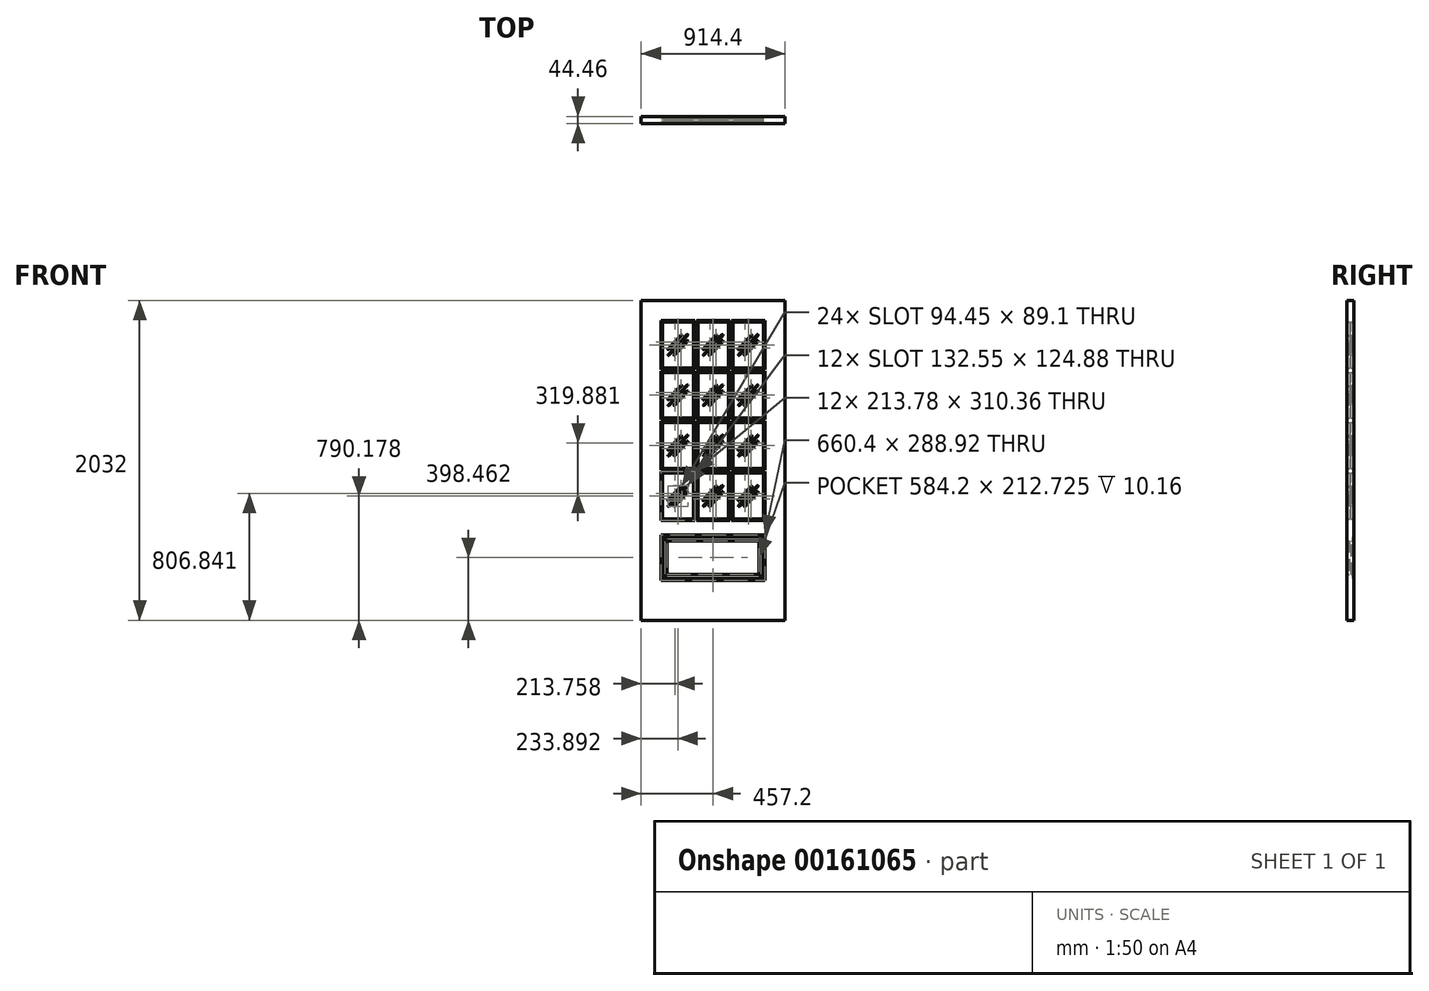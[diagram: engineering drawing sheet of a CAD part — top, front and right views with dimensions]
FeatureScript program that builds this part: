
annotation { "Feature Type Name" : "Feature", "Feature Type Description" : "" }
export const myFeature = defineFeature(function(context is Context, id is Id, definition is map)
    precondition{}
    {
        {
            var Q0;
            Q0=qCreatedBy(makeId("Front.planeOp"),FACE);
            var sketch = newSketch(context, id + "F0", { "sketchPlane" : qUnion([Q0])});
            skLineSegment(sketch, "E0.bottom", {"start": v(0, 2032) * mm, "end": v(914.4, 2032) * mm});
            skLineSegment(sketch, "E0.top", {"start": v(0, 0) * mm, "end": v(914.4, 0) * mm});
            skLineSegment(sketch, "E0.left", {"start": v(0, 2032) * mm, "end": v(0, 0) * mm});
            skLineSegment(sketch, "E0.right", {"start": v(914.4, 2032) * mm, "end": v(914.4, 0) * mm});
            skLineSegment(sketch, "E1.bottom", {"start": v(787.4, 254) * mm, "end": v(127, 254) * mm});
            skLineSegment(sketch, "E1.top", {"start": v(787.4, 542.93) * mm, "end": v(127, 542.93) * mm});
            skLineSegment(sketch, "E1.left", {"start": v(787.4, 254) * mm, "end": v(787.4, 542.93) * mm});
            skLineSegment(sketch, "E1.right", {"start": v(127, 254) * mm, "end": v(127, 542.93) * mm});
            skLineSegment(sketch, "E2.bottom", {"start": v(787.4, 635) * mm, "end": v(573.62, 635) * mm});
            skLineSegment(sketch, "E2.top", {"start": v(787.4, 945.36) * mm, "end": v(573.62, 945.36) * mm});
            skLineSegment(sketch, "E2.left", {"start": v(787.4, 635) * mm, "end": v(787.4, 945.36) * mm});
            skLineSegment(sketch, "E2.right", {"start": v(573.62, 635) * mm, "end": v(573.62, 945.36) * mm});
            skLineSegment(sketch, "E3.bottom", {"start": v(583.14, 935.83) * mm, "end": v(777.88, 935.83) * mm});
            skLineSegment(sketch, "E3.top", {"start": v(583.14, 644.53) * mm, "end": v(777.88, 644.53) * mm});
            skLineSegment(sketch, "E3.left", {"start": v(583.14, 935.83) * mm, "end": v(583.14, 644.53) * mm});
            skLineSegment(sketch, "E3.right", {"start": v(777.88, 935.83) * mm, "end": v(777.88, 644.53) * mm});
            skLineSegment(sketch, "E4", {"start": v(777.88, 935.83) * mm, "end": v(787.4, 945.36) * mm});
            skLineSegment(sketch, "E5", {"start": v(777.88, 644.52) * mm, "end": v(787.4, 635) * mm});
            skLineSegment(sketch, "E6", {"start": v(583.14, 644.53) * mm, "end": v(573.62, 635) * mm});
            skLineSegment(sketch, "E7", {"start": v(583.14, 935.83) * mm, "end": v(573.62, 945.36) * mm});
            skLineSegment(sketch, "E8", {"start": v(621.24, 727.08) * mm, "end": v(739.78, 853.28) * mm});
            skLineSegment(sketch, "E9", {"start": v(739.78, 815.18) * mm, "end": v(657.03, 727.08) * mm});
            skLineSegment(sketch, "E10.MirrorCS", {"start": v(701.75, 850.9) * mm, "end": v(619, 762.79) * mm});
            skLineSegment(sketch, "E11.0.1.1", {"start": v(583.14, 964.4) * mm, "end": v(777.88, 964.4) * mm});
            skLineSegment(sketch, "E11.0.1.2", {"start": v(701.75, 1170.78) * mm, "end": v(619, 1082.67) * mm});
            skLineSegment(sketch, "E11.0.1.3", {"start": v(787.4, 954.88) * mm, "end": v(573.62, 954.88) * mm});
            skLineSegment(sketch, "E11.0.1.4", {"start": v(583.14, 1255.71) * mm, "end": v(777.88, 1255.71) * mm});
            skLineSegment(sketch, "E11.0.1.7", {"start": v(621.24, 1046.96) * mm, "end": v(739.78, 1173.16) * mm});
            skLineSegment(sketch, "E11.0.1.9", {"start": v(573.62, 954.88) * mm, "end": v(573.62, 1265.24) * mm});
            skLineSegment(sketch, "E11.0.1.10", {"start": v(777.88, 1255.71) * mm, "end": v(777.88, 964.4) * mm});
            skLineSegment(sketch, "E11.0.1.11", {"start": v(787.4, 1265.24) * mm, "end": v(573.62, 1265.24) * mm});
            skLineSegment(sketch, "E11.0.1.12", {"start": v(739.78, 1135.06) * mm, "end": v(657.03, 1046.96) * mm});
            skLineSegment(sketch, "E11.0.1.13", {"start": v(787.4, 954.88) * mm, "end": v(787.4, 1265.24) * mm});
            skLineSegment(sketch, "E11.0.1.14", {"start": v(583.14, 1255.71) * mm, "end": v(583.14, 964.4) * mm});
            skLineSegment(sketch, "E11.0.1.15", {"start": v(777.88, 964.4) * mm, "end": v(787.4, 954.88) * mm});
            skLineSegment(sketch, "E11.0.1.16", {"start": v(777.87, 1255.71) * mm, "end": v(787.4, 1265.24) * mm});
            skLineSegment(sketch, "E11.0.1.17", {"start": v(583.14, 1255.71) * mm, "end": v(573.62, 1265.24) * mm});
            skLineSegment(sketch, "E11.0.1.18", {"start": v(583.14, 964.4) * mm, "end": v(573.62, 954.88) * mm});
            skLineSegment(sketch, "E11.0.2.1", {"start": v(583.14, 1284.29) * mm, "end": v(777.88, 1284.29) * mm});
            skLineSegment(sketch, "E11.0.2.2", {"start": v(701.75, 1490.66) * mm, "end": v(619, 1402.55) * mm});
            skLineSegment(sketch, "E11.0.2.3", {"start": v(787.4, 1274.76) * mm, "end": v(573.62, 1274.76) * mm});
            skLineSegment(sketch, "E11.0.2.4", {"start": v(583.14, 1575.6) * mm, "end": v(777.88, 1575.6) * mm});
            skLineSegment(sketch, "E11.0.2.7", {"start": v(621.24, 1366.84) * mm, "end": v(739.78, 1493.04) * mm});
            skLineSegment(sketch, "E11.0.2.9", {"start": v(573.62, 1274.76) * mm, "end": v(573.62, 1585.12) * mm});
            skLineSegment(sketch, "E11.0.2.10", {"start": v(777.88, 1575.6) * mm, "end": v(777.88, 1284.29) * mm});
            skLineSegment(sketch, "E11.0.2.11", {"start": v(787.4, 1585.12) * mm, "end": v(573.62, 1585.12) * mm});
            skLineSegment(sketch, "E11.0.2.12", {"start": v(739.77, 1454.94) * mm, "end": v(657.03, 1366.84) * mm});
            skLineSegment(sketch, "E11.0.2.13", {"start": v(787.4, 1274.76) * mm, "end": v(787.4, 1585.12) * mm});
            skLineSegment(sketch, "E11.0.2.14", {"start": v(583.14, 1575.6) * mm, "end": v(583.14, 1284.29) * mm});
            skLineSegment(sketch, "E11.0.2.15", {"start": v(777.88, 1284.29) * mm, "end": v(787.4, 1274.76) * mm});
            skLineSegment(sketch, "E11.0.2.16", {"start": v(777.87, 1575.6) * mm, "end": v(787.4, 1585.12) * mm});
            skLineSegment(sketch, "E11.0.2.17", {"start": v(583.14, 1575.6) * mm, "end": v(573.62, 1585.12) * mm});
            skLineSegment(sketch, "E11.0.2.18", {"start": v(583.14, 1284.29) * mm, "end": v(573.62, 1274.76) * mm});
            skLineSegment(sketch, "E11.1.0.1", {"start": v(359.83, 644.53) * mm, "end": v(554.57, 644.53) * mm});
            skLineSegment(sketch, "E11.1.0.2", {"start": v(478.44, 850.9) * mm, "end": v(395.7, 762.79) * mm});
            skLineSegment(sketch, "E11.1.0.3", {"start": v(564.1, 635) * mm, "end": v(350.3, 635) * mm});
            skLineSegment(sketch, "E11.1.0.4", {"start": v(359.83, 935.83) * mm, "end": v(554.57, 935.83) * mm});
            skLineSegment(sketch, "E11.1.0.7", {"start": v(397.93, 727.08) * mm, "end": v(516.47, 853.28) * mm});
            skLineSegment(sketch, "E11.1.0.9", {"start": v(350.3, 635) * mm, "end": v(350.3, 945.36) * mm});
            skLineSegment(sketch, "E11.1.0.10", {"start": v(554.57, 935.83) * mm, "end": v(554.57, 644.52) * mm});
            skLineSegment(sketch, "E11.1.0.11", {"start": v(564.1, 945.36) * mm, "end": v(350.3, 945.36) * mm});
            skLineSegment(sketch, "E11.1.0.12", {"start": v(516.47, 815.18) * mm, "end": v(433.72, 727.08) * mm});
            skLineSegment(sketch, "E11.1.0.13", {"start": v(564.1, 635) * mm, "end": v(564.1, 945.36) * mm});
            skLineSegment(sketch, "E11.1.0.14", {"start": v(359.83, 935.83) * mm, "end": v(359.83, 644.52) * mm});
            skLineSegment(sketch, "E11.1.0.15", {"start": v(554.57, 644.52) * mm, "end": v(564.1, 635) * mm});
            skLineSegment(sketch, "E11.1.0.16", {"start": v(554.57, 935.83) * mm, "end": v(564.1, 945.36) * mm});
            skLineSegment(sketch, "E11.1.0.17", {"start": v(359.83, 935.83) * mm, "end": v(350.3, 945.36) * mm});
            skLineSegment(sketch, "E11.1.0.18", {"start": v(359.83, 644.52) * mm, "end": v(350.3, 635) * mm});
            skLineSegment(sketch, "E11.1.1.1", {"start": v(359.83, 964.4) * mm, "end": v(554.57, 964.4) * mm});
            skLineSegment(sketch, "E11.1.1.2", {"start": v(478.44, 1170.78) * mm, "end": v(395.7, 1082.67) * mm});
            skLineSegment(sketch, "E11.1.1.3", {"start": v(564.1, 954.88) * mm, "end": v(350.3, 954.88) * mm});
            skLineSegment(sketch, "E11.1.1.4", {"start": v(359.83, 1255.71) * mm, "end": v(554.57, 1255.71) * mm});
            skLineSegment(sketch, "E11.1.1.7", {"start": v(397.93, 1046.96) * mm, "end": v(516.47, 1173.16) * mm});
            skLineSegment(sketch, "E11.1.1.9", {"start": v(350.3, 954.88) * mm, "end": v(350.3, 1265.24) * mm});
            skLineSegment(sketch, "E11.1.1.10", {"start": v(554.57, 1255.71) * mm, "end": v(554.57, 964.4) * mm});
            skLineSegment(sketch, "E11.1.1.11", {"start": v(564.1, 1265.24) * mm, "end": v(350.3, 1265.24) * mm});
            skLineSegment(sketch, "E11.1.1.12", {"start": v(516.47, 1135.06) * mm, "end": v(433.72, 1046.96) * mm});
            skLineSegment(sketch, "E11.1.1.13", {"start": v(564.1, 954.88) * mm, "end": v(564.1, 1265.24) * mm});
            skLineSegment(sketch, "E11.1.1.14", {"start": v(359.83, 1255.71) * mm, "end": v(359.83, 964.4) * mm});
            skLineSegment(sketch, "E11.1.1.15", {"start": v(554.57, 964.4) * mm, "end": v(564.1, 954.88) * mm});
            skLineSegment(sketch, "E11.1.1.16", {"start": v(554.57, 1255.71) * mm, "end": v(564.1, 1265.24) * mm});
            skLineSegment(sketch, "E11.1.1.17", {"start": v(359.83, 1255.71) * mm, "end": v(350.3, 1265.24) * mm});
            skLineSegment(sketch, "E11.1.1.18", {"start": v(359.83, 964.4) * mm, "end": v(350.3, 954.88) * mm});
            skLineSegment(sketch, "E11.1.2.1", {"start": v(359.83, 1284.29) * mm, "end": v(554.57, 1284.29) * mm});
            skLineSegment(sketch, "E11.1.2.2", {"start": v(478.44, 1490.66) * mm, "end": v(395.7, 1402.55) * mm});
            skLineSegment(sketch, "E11.1.2.3", {"start": v(564.1, 1274.76) * mm, "end": v(350.3, 1274.76) * mm});
            skLineSegment(sketch, "E11.1.2.4", {"start": v(359.83, 1575.6) * mm, "end": v(554.57, 1575.6) * mm});
            skLineSegment(sketch, "E11.1.2.7", {"start": v(397.93, 1366.84) * mm, "end": v(516.47, 1493.04) * mm});
            skLineSegment(sketch, "E11.1.2.9", {"start": v(350.3, 1274.76) * mm, "end": v(350.3, 1585.12) * mm});
            skLineSegment(sketch, "E11.1.2.10", {"start": v(554.57, 1575.6) * mm, "end": v(554.57, 1284.29) * mm});
            skLineSegment(sketch, "E11.1.2.11", {"start": v(564.1, 1585.12) * mm, "end": v(350.3, 1585.12) * mm});
            skLineSegment(sketch, "E11.1.2.12", {"start": v(516.47, 1454.94) * mm, "end": v(433.72, 1366.84) * mm});
            skLineSegment(sketch, "E11.1.2.13", {"start": v(564.1, 1274.76) * mm, "end": v(564.1, 1585.12) * mm});
            skLineSegment(sketch, "E11.1.2.14", {"start": v(359.83, 1575.6) * mm, "end": v(359.83, 1284.29) * mm});
            skLineSegment(sketch, "E11.1.2.15", {"start": v(554.57, 1284.29) * mm, "end": v(564.1, 1274.76) * mm});
            skLineSegment(sketch, "E11.1.2.16", {"start": v(554.57, 1575.6) * mm, "end": v(564.1, 1585.12) * mm});
            skLineSegment(sketch, "E11.1.2.17", {"start": v(359.83, 1575.6) * mm, "end": v(350.3, 1585.12) * mm});
            skLineSegment(sketch, "E11.1.2.18", {"start": v(359.83, 1284.29) * mm, "end": v(350.3, 1274.76) * mm});
            skLineSegment(sketch, "E11.2.0.1", {"start": v(136.53, 644.53) * mm, "end": v(331.26, 644.53) * mm});
            skLineSegment(sketch, "E11.2.0.2", {"start": v(255.13, 850.9) * mm, "end": v(172.38, 762.79) * mm});
            skLineSegment(sketch, "E11.2.0.3", {"start": v(340.78, 635) * mm, "end": v(127, 635) * mm});
            skLineSegment(sketch, "E11.2.0.4", {"start": v(136.52, 935.83) * mm, "end": v(331.26, 935.83) * mm});
            skLineSegment(sketch, "E11.2.0.7", {"start": v(174.63, 727.08) * mm, "end": v(293.16, 853.28) * mm});
            skLineSegment(sketch, "E11.2.0.9", {"start": v(127, 635) * mm, "end": v(127, 945.36) * mm});
            skLineSegment(sketch, "E11.2.0.10", {"start": v(331.26, 935.83) * mm, "end": v(331.26, 644.52) * mm});
            skLineSegment(sketch, "E11.2.0.11", {"start": v(340.78, 945.36) * mm, "end": v(127, 945.36) * mm});
            skLineSegment(sketch, "E11.2.0.12", {"start": v(293.16, 815.18) * mm, "end": v(210.4, 727.08) * mm});
            skLineSegment(sketch, "E11.2.0.13", {"start": v(340.78, 635) * mm, "end": v(340.78, 945.36) * mm});
            skLineSegment(sketch, "E11.2.0.14", {"start": v(136.52, 935.83) * mm, "end": v(136.52, 644.52) * mm});
            skLineSegment(sketch, "E11.2.0.15", {"start": v(331.26, 644.52) * mm, "end": v(340.78, 635) * mm});
            skLineSegment(sketch, "E11.2.0.16", {"start": v(331.26, 935.83) * mm, "end": v(340.78, 945.36) * mm});
            skLineSegment(sketch, "E11.2.0.17", {"start": v(136.52, 935.83) * mm, "end": v(127, 945.36) * mm});
            skLineSegment(sketch, "E11.2.0.18", {"start": v(136.52, 644.52) * mm, "end": v(127, 635) * mm});
            skLineSegment(sketch, "E11.2.1.1", {"start": v(136.52, 964.4) * mm, "end": v(331.26, 964.4) * mm});
            skLineSegment(sketch, "E11.2.1.2", {"start": v(255.13, 1170.78) * mm, "end": v(172.38, 1082.67) * mm});
            skLineSegment(sketch, "E11.2.1.3", {"start": v(340.78, 954.88) * mm, "end": v(127, 954.88) * mm});
            skLineSegment(sketch, "E11.2.1.4", {"start": v(136.52, 1255.71) * mm, "end": v(331.26, 1255.71) * mm});
            skLineSegment(sketch, "E11.2.1.7", {"start": v(174.63, 1046.96) * mm, "end": v(293.16, 1173.16) * mm});
            skLineSegment(sketch, "E11.2.1.9", {"start": v(127, 954.88) * mm, "end": v(127, 1265.24) * mm});
            skLineSegment(sketch, "E11.2.1.10", {"start": v(331.26, 1255.71) * mm, "end": v(331.26, 964.4) * mm});
            skLineSegment(sketch, "E11.2.1.11", {"start": v(340.78, 1265.24) * mm, "end": v(127, 1265.24) * mm});
            skLineSegment(sketch, "E11.2.1.12", {"start": v(293.16, 1135.06) * mm, "end": v(210.4, 1046.96) * mm});
            skLineSegment(sketch, "E11.2.1.13", {"start": v(340.78, 954.88) * mm, "end": v(340.78, 1265.24) * mm});
            skLineSegment(sketch, "E11.2.1.14", {"start": v(136.52, 1255.71) * mm, "end": v(136.52, 964.4) * mm});
            skLineSegment(sketch, "E11.2.1.15", {"start": v(331.26, 964.4) * mm, "end": v(340.78, 954.88) * mm});
            skLineSegment(sketch, "E11.2.1.16", {"start": v(331.26, 1255.71) * mm, "end": v(340.78, 1265.24) * mm});
            skLineSegment(sketch, "E11.2.1.17", {"start": v(136.52, 1255.71) * mm, "end": v(127, 1265.24) * mm});
            skLineSegment(sketch, "E11.2.1.18", {"start": v(136.52, 964.4) * mm, "end": v(127, 954.88) * mm});
            skLineSegment(sketch, "E11.2.2.1", {"start": v(136.52, 1284.29) * mm, "end": v(331.26, 1284.29) * mm});
            skLineSegment(sketch, "E11.2.2.2", {"start": v(255.13, 1490.66) * mm, "end": v(172.38, 1402.55) * mm});
            skLineSegment(sketch, "E11.2.2.3", {"start": v(340.78, 1274.76) * mm, "end": v(127, 1274.76) * mm});
            skLineSegment(sketch, "E11.2.2.4", {"start": v(136.52, 1575.6) * mm, "end": v(331.26, 1575.6) * mm});
            skLineSegment(sketch, "E11.2.2.7", {"start": v(174.63, 1366.84) * mm, "end": v(293.16, 1493.04) * mm});
            skLineSegment(sketch, "E11.2.2.9", {"start": v(127, 1274.76) * mm, "end": v(127, 1585.12) * mm});
            skLineSegment(sketch, "E11.2.2.10", {"start": v(331.26, 1575.6) * mm, "end": v(331.26, 1284.29) * mm});
            skLineSegment(sketch, "E11.2.2.11", {"start": v(340.78, 1585.12) * mm, "end": v(127, 1585.12) * mm});
            skLineSegment(sketch, "E11.2.2.12", {"start": v(293.16, 1454.94) * mm, "end": v(210.4, 1366.84) * mm});
            skLineSegment(sketch, "E11.2.2.13", {"start": v(340.78, 1274.76) * mm, "end": v(340.78, 1585.12) * mm});
            skLineSegment(sketch, "E11.2.2.14", {"start": v(136.52, 1575.6) * mm, "end": v(136.52, 1284.29) * mm});
            skLineSegment(sketch, "E11.2.2.15", {"start": v(331.26, 1284.29) * mm, "end": v(340.78, 1274.76) * mm});
            skLineSegment(sketch, "E11.2.2.16", {"start": v(331.26, 1575.6) * mm, "end": v(340.78, 1585.12) * mm});
            skLineSegment(sketch, "E11.2.2.17", {"start": v(136.52, 1575.6) * mm, "end": v(127, 1585.12) * mm});
            skLineSegment(sketch, "E11.2.2.18", {"start": v(136.52, 1284.29) * mm, "end": v(127, 1274.76) * mm});
            skLineSegment(sketch, "E11.direction1", {"start": v(573.62, 635) * mm, "end": v(350.3, 635) * mm, "construction": true});
            skLineSegment(sketch, "E11.direction2", {"start": v(573.62, 635) * mm, "end": v(573.62, 954.88) * mm, "construction": true});
            skLineSegment(sketch, "E12.3.0.3", {"start": v(583.14, 1604.17) * mm, "end": v(777.88, 1604.17) * mm});
            skLineSegment(sketch, "E12.6.0.3", {"start": v(701.75, 1810.54) * mm, "end": v(619, 1722.43) * mm});
            skLineSegment(sketch, "E12.9.0.3", {"start": v(787.4, 1594.64) * mm, "end": v(573.62, 1594.64) * mm});
            skLineSegment(sketch, "E12.12.0.3", {"start": v(583.14, 1895.48) * mm, "end": v(777.88, 1895.48) * mm});
            skLineSegment(sketch, "E12.21.0.3", {"start": v(621.24, 1686.72) * mm, "end": v(739.77, 1812.92) * mm});
            skLineSegment(sketch, "E12.27.0.3", {"start": v(573.62, 1594.64) * mm, "end": v(573.62, 1905) * mm});
            skLineSegment(sketch, "E12.30.0.3", {"start": v(777.88, 1895.48) * mm, "end": v(777.88, 1604.17) * mm});
            skLineSegment(sketch, "E12.33.0.3", {"start": v(787.4, 1905) * mm, "end": v(573.62, 1905) * mm});
            skLineSegment(sketch, "E12.36.0.3", {"start": v(739.77, 1774.82) * mm, "end": v(657.03, 1686.72) * mm});
            skLineSegment(sketch, "E12.39.0.3", {"start": v(787.4, 1594.64) * mm, "end": v(787.4, 1905) * mm});
            skLineSegment(sketch, "E12.42.0.3", {"start": v(583.14, 1895.48) * mm, "end": v(583.14, 1604.17) * mm});
            skLineSegment(sketch, "E12.45.0.3", {"start": v(777.88, 1604.17) * mm, "end": v(787.4, 1594.64) * mm});
            skLineSegment(sketch, "E12.48.0.3", {"start": v(777.88, 1895.47) * mm, "end": v(787.4, 1905) * mm});
            skLineSegment(sketch, "E12.51.0.3", {"start": v(583.14, 1895.48) * mm, "end": v(573.62, 1905) * mm});
            skLineSegment(sketch, "E12.54.0.3", {"start": v(583.14, 1604.17) * mm, "end": v(573.62, 1594.64) * mm});
            skLineSegment(sketch, "E12.3.1.3", {"start": v(359.83, 1604.17) * mm, "end": v(554.57, 1604.17) * mm});
            skLineSegment(sketch, "E12.6.1.3", {"start": v(478.44, 1810.54) * mm, "end": v(395.7, 1722.43) * mm});
            skLineSegment(sketch, "E12.9.1.3", {"start": v(564.1, 1594.64) * mm, "end": v(350.3, 1594.64) * mm});
            skLineSegment(sketch, "E12.12.1.3", {"start": v(359.83, 1895.48) * mm, "end": v(554.57, 1895.48) * mm});
            skLineSegment(sketch, "E12.21.1.3", {"start": v(397.93, 1686.72) * mm, "end": v(516.47, 1812.92) * mm});
            skLineSegment(sketch, "E12.27.1.3", {"start": v(350.3, 1594.64) * mm, "end": v(350.3, 1905) * mm});
            skLineSegment(sketch, "E12.30.1.3", {"start": v(554.57, 1895.48) * mm, "end": v(554.57, 1604.17) * mm});
            skLineSegment(sketch, "E12.33.1.3", {"start": v(564.1, 1905) * mm, "end": v(350.3, 1905) * mm});
            skLineSegment(sketch, "E12.36.1.3", {"start": v(516.47, 1774.82) * mm, "end": v(433.72, 1686.72) * mm});
            skLineSegment(sketch, "E12.39.1.3", {"start": v(564.1, 1594.64) * mm, "end": v(564.1, 1905) * mm});
            skLineSegment(sketch, "E12.42.1.3", {"start": v(359.83, 1895.48) * mm, "end": v(359.83, 1604.17) * mm});
            skLineSegment(sketch, "E12.45.1.3", {"start": v(554.57, 1604.17) * mm, "end": v(564.1, 1594.64) * mm});
            skLineSegment(sketch, "E12.48.1.3", {"start": v(554.57, 1895.47) * mm, "end": v(564.1, 1905) * mm});
            skLineSegment(sketch, "E12.51.1.3", {"start": v(359.83, 1895.48) * mm, "end": v(350.3, 1905) * mm});
            skLineSegment(sketch, "E12.54.1.3", {"start": v(359.83, 1604.17) * mm, "end": v(350.3, 1594.64) * mm});
            skLineSegment(sketch, "E12.3.2.3", {"start": v(136.52, 1604.17) * mm, "end": v(331.26, 1604.17) * mm});
            skLineSegment(sketch, "E12.6.2.3", {"start": v(255.13, 1810.54) * mm, "end": v(172.38, 1722.43) * mm});
            skLineSegment(sketch, "E12.9.2.3", {"start": v(340.78, 1594.64) * mm, "end": v(127, 1594.64) * mm});
            skLineSegment(sketch, "E12.12.2.3", {"start": v(136.52, 1895.48) * mm, "end": v(331.26, 1895.48) * mm});
            skLineSegment(sketch, "E12.21.2.3", {"start": v(174.63, 1686.72) * mm, "end": v(293.16, 1812.92) * mm});
            skLineSegment(sketch, "E12.27.2.3", {"start": v(127, 1594.64) * mm, "end": v(127, 1905) * mm});
            skLineSegment(sketch, "E12.30.2.3", {"start": v(331.26, 1895.48) * mm, "end": v(331.26, 1604.17) * mm});
            skLineSegment(sketch, "E12.33.2.3", {"start": v(340.78, 1905) * mm, "end": v(127, 1905) * mm});
            skLineSegment(sketch, "E12.36.2.3", {"start": v(293.16, 1774.82) * mm, "end": v(210.4, 1686.72) * mm});
            skLineSegment(sketch, "E12.39.2.3", {"start": v(340.78, 1594.64) * mm, "end": v(340.78, 1905) * mm});
            skLineSegment(sketch, "E12.42.2.3", {"start": v(136.52, 1895.48) * mm, "end": v(136.52, 1604.17) * mm});
            skLineSegment(sketch, "E12.45.2.3", {"start": v(331.26, 1604.17) * mm, "end": v(340.78, 1594.64) * mm});
            skLineSegment(sketch, "E12.48.2.3", {"start": v(331.26, 1895.47) * mm, "end": v(340.78, 1905) * mm});
            skLineSegment(sketch, "E12.51.2.3", {"start": v(136.52, 1895.48) * mm, "end": v(127, 1905) * mm});
            skLineSegment(sketch, "E12.54.2.3", {"start": v(136.52, 1604.17) * mm, "end": v(127, 1594.64) * mm});
            skLineSegment(sketch, "E13.0", {"start": v(774.7, 530.22) * mm, "end": v(139.7, 530.22) * mm});
            skLineSegment(sketch, "E13.1", {"start": v(774.7, 266.7) * mm, "end": v(774.7, 530.22) * mm});
            skLineSegment(sketch, "E13.2", {"start": v(774.7, 266.7) * mm, "end": v(139.7, 266.7) * mm});
            skLineSegment(sketch, "E13.3", {"start": v(139.7, 266.7) * mm, "end": v(139.7, 530.22) * mm});
            skLineSegment(sketch, "E14.0", {"start": v(749.3, 292.1) * mm, "end": v(165.1, 292.1) * mm});
            skLineSegment(sketch, "E14.1", {"start": v(749.3, 292.1) * mm, "end": v(749.3, 504.83) * mm});
            skLineSegment(sketch, "E14.2", {"start": v(749.3, 504.83) * mm, "end": v(165.1, 504.83) * mm});
            skLineSegment(sketch, "E14.3", {"start": v(165.1, 292.1) * mm, "end": v(165.1, 504.83) * mm});
            skSolve(sketch);
        }
        {
            var Q0;
            Q0=qCreatedBy(makeId("Front.planeOp"),FACE);
            var sketch = newSketch(context, id + "F1", { "sketchPlane" : qUnion([Q0])});
            skLineSegment(sketch, "E15.bottom", {"start": v(0, 2032) * mm, "end": v(914.4, 2032) * mm});
            skLineSegment(sketch, "E15.top", {"start": v(0, 0) * mm, "end": v(914.4, 0) * mm});
            skLineSegment(sketch, "E15.left", {"start": v(0, 2032) * mm, "end": v(0, 0) * mm});
            skLineSegment(sketch, "E15.right", {"start": v(914.4, 2032) * mm, "end": v(914.4, 0) * mm});
            skLineSegment(sketch, "E16.bottom", {"start": v(127, 542.93) * mm, "end": v(787.4, 542.93) * mm});
            skLineSegment(sketch, "E16.top", {"start": v(127, 254) * mm, "end": v(787.4, 254) * mm});
            skLineSegment(sketch, "E16.left", {"start": v(127, 542.93) * mm, "end": v(127, 254) * mm});
            skLineSegment(sketch, "E16.right", {"start": v(787.4, 542.93) * mm, "end": v(787.4, 254) * mm});
            skLineSegment(sketch, "E17.bottom", {"start": v(127, 635) * mm, "end": v(340.78, 635) * mm});
            skLineSegment(sketch, "E17.top", {"start": v(127, 945.36) * mm, "end": v(340.78, 945.36) * mm});
            skLineSegment(sketch, "E17.left", {"start": v(127, 635) * mm, "end": v(127, 945.36) * mm});
            skLineSegment(sketch, "E17.right", {"start": v(340.78, 635) * mm, "end": v(340.78, 945.36) * mm});
            skLineSegment(sketch, "E18.bottom", {"start": v(350.3, 945.36) * mm, "end": v(564.1, 945.36) * mm});
            skLineSegment(sketch, "E18.top", {"start": v(350.3, 635) * mm, "end": v(564.1, 635) * mm});
            skLineSegment(sketch, "E18.left", {"start": v(350.3, 945.36) * mm, "end": v(350.3, 635) * mm});
            skLineSegment(sketch, "E18.right", {"start": v(564.1, 945.36) * mm, "end": v(564.1, 635) * mm});
            skLineSegment(sketch, "E19.bottom", {"start": v(573.62, 945.36) * mm, "end": v(787.4, 945.36) * mm});
            skLineSegment(sketch, "E19.top", {"start": v(573.62, 635) * mm, "end": v(787.4, 635) * mm});
            skLineSegment(sketch, "E19.left", {"start": v(573.62, 945.36) * mm, "end": v(573.62, 635) * mm});
            skLineSegment(sketch, "E19.right", {"start": v(787.4, 945.36) * mm, "end": v(787.4, 635) * mm});
            skLineSegment(sketch, "E20.bottom", {"start": v(573.62, 954.88) * mm, "end": v(787.4, 954.88) * mm});
            skLineSegment(sketch, "E20.top", {"start": v(573.62, 1265.24) * mm, "end": v(787.4, 1265.24) * mm});
            skLineSegment(sketch, "E20.left", {"start": v(573.62, 954.88) * mm, "end": v(573.62, 1265.24) * mm});
            skLineSegment(sketch, "E20.right", {"start": v(787.4, 954.88) * mm, "end": v(787.4, 1265.24) * mm});
            skLineSegment(sketch, "E21.bottom", {"start": v(350.3, 1265.24) * mm, "end": v(564.1, 1265.24) * mm});
            skLineSegment(sketch, "E21.top", {"start": v(350.3, 954.88) * mm, "end": v(564.1, 954.88) * mm});
            skLineSegment(sketch, "E21.left", {"start": v(350.3, 1265.24) * mm, "end": v(350.3, 954.88) * mm});
            skLineSegment(sketch, "E21.right", {"start": v(564.1, 1265.24) * mm, "end": v(564.1, 954.88) * mm});
            skLineSegment(sketch, "E22.bottom", {"start": v(340.78, 1265.24) * mm, "end": v(127, 1265.24) * mm});
            skLineSegment(sketch, "E22.top", {"start": v(340.78, 954.88) * mm, "end": v(127, 954.88) * mm});
            skLineSegment(sketch, "E22.left", {"start": v(340.78, 1265.24) * mm, "end": v(340.78, 954.88) * mm});
            skLineSegment(sketch, "E22.right", {"start": v(127, 1265.24) * mm, "end": v(127, 954.88) * mm});
            skLineSegment(sketch, "E23.bottom", {"start": v(127, 1274.76) * mm, "end": v(340.78, 1274.76) * mm});
            skLineSegment(sketch, "E23.top", {"start": v(127, 1585.12) * mm, "end": v(340.78, 1585.12) * mm});
            skLineSegment(sketch, "E23.left", {"start": v(127, 1274.76) * mm, "end": v(127, 1585.12) * mm});
            skLineSegment(sketch, "E23.right", {"start": v(340.78, 1274.76) * mm, "end": v(340.78, 1585.12) * mm});
            skLineSegment(sketch, "E24.bottom", {"start": v(350.3, 1585.12) * mm, "end": v(564.1, 1585.12) * mm});
            skLineSegment(sketch, "E24.top", {"start": v(350.3, 1274.76) * mm, "end": v(564.1, 1274.76) * mm});
            skLineSegment(sketch, "E24.left", {"start": v(350.3, 1585.12) * mm, "end": v(350.3, 1274.76) * mm});
            skLineSegment(sketch, "E24.right", {"start": v(564.1, 1585.12) * mm, "end": v(564.1, 1274.76) * mm});
            skLineSegment(sketch, "E25.bottom", {"start": v(573.62, 1585.12) * mm, "end": v(787.4, 1585.12) * mm});
            skLineSegment(sketch, "E25.top", {"start": v(573.62, 1274.76) * mm, "end": v(787.4, 1274.76) * mm});
            skLineSegment(sketch, "E25.left", {"start": v(573.62, 1585.12) * mm, "end": v(573.62, 1274.76) * mm});
            skLineSegment(sketch, "E25.right", {"start": v(787.4, 1585.12) * mm, "end": v(787.4, 1274.76) * mm});
            skLineSegment(sketch, "E26.bottom", {"start": v(573.62, 1594.64) * mm, "end": v(787.4, 1594.64) * mm});
            skLineSegment(sketch, "E26.top", {"start": v(573.62, 1905) * mm, "end": v(787.4, 1905) * mm});
            skLineSegment(sketch, "E26.left", {"start": v(573.62, 1594.64) * mm, "end": v(573.62, 1905) * mm});
            skLineSegment(sketch, "E26.right", {"start": v(787.4, 1594.64) * mm, "end": v(787.4, 1905) * mm});
            skLineSegment(sketch, "E27.bottom", {"start": v(564.1, 1905) * mm, "end": v(350.3, 1905) * mm});
            skLineSegment(sketch, "E27.top", {"start": v(564.1, 1594.64) * mm, "end": v(350.3, 1594.64) * mm});
            skLineSegment(sketch, "E27.left", {"start": v(564.1, 1905) * mm, "end": v(564.1, 1594.64) * mm});
            skLineSegment(sketch, "E27.right", {"start": v(350.3, 1905) * mm, "end": v(350.3, 1594.64) * mm});
            skLineSegment(sketch, "E28.bottom", {"start": v(340.78, 1594.64) * mm, "end": v(127, 1594.64) * mm});
            skLineSegment(sketch, "E28.top", {"start": v(340.78, 1905) * mm, "end": v(127, 1905) * mm});
            skLineSegment(sketch, "E28.left", {"start": v(340.78, 1594.64) * mm, "end": v(340.78, 1905) * mm});
            skLineSegment(sketch, "E28.right", {"start": v(127, 1594.64) * mm, "end": v(127, 1905) * mm});
            skSolve(sketch);
        }
        {
            var Q0;
            Q0=qSketchRegion(id+"F1",true);
            extrude(context, id + "F2", {"entities" : qUnion([Q0]), "depth" : 22.22 * mm, "hasSecondDirection" : true, "secondDirectionOppositeDirection" : true, "secondDirectionDepth" : 22.22 * mm});
        }
        {
            var Q0;
            Q0=qCreatedBy(makeId("Front.planeOp"),FACE);
            var sketch = newSketch(context, id + "F3", { "sketchPlane" : qUnion([Q0])});
            skLineSegment(sketch, "E29.0", {"start": v(787.4, 1594.64) * mm, "end": v(787.4, 1905) * mm});
            skLineSegment(sketch, "E30.0", {"start": v(777.88, 1895.47) * mm, "end": v(787.4, 1905) * mm});
            skLineSegment(sketch, "E31.0", {"start": v(777.88, 1895.48) * mm, "end": v(777.88, 1604.17) * mm});
            skLineSegment(sketch, "E32.0", {"start": v(777.88, 1604.17) * mm, "end": v(787.4, 1594.64) * mm});
            skLineSegment(sketch, "E33.0", {"start": v(583.14, 1604.17) * mm, "end": v(573.62, 1594.64) * mm});
            skLineSegment(sketch, "E34.0", {"start": v(583.14, 1895.48) * mm, "end": v(583.14, 1604.17) * mm});
            skLineSegment(sketch, "E35.0", {"start": v(583.14, 1895.48) * mm, "end": v(573.62, 1905) * mm});
            skLineSegment(sketch, "E36.0", {"start": v(573.62, 1594.64) * mm, "end": v(573.62, 1905) * mm});
            skLineSegment(sketch, "E37.0", {"start": v(564.1, 1594.64) * mm, "end": v(564.1, 1905) * mm});
            skLineSegment(sketch, "E38.0", {"start": v(554.57, 1895.47) * mm, "end": v(564.1, 1905) * mm});
            skLineSegment(sketch, "E39.0", {"start": v(554.57, 1895.48) * mm, "end": v(554.57, 1604.17) * mm});
            skLineSegment(sketch, "E40.0", {"start": v(554.57, 1604.17) * mm, "end": v(564.1, 1594.64) * mm});
            skLineSegment(sketch, "E41.0", {"start": v(359.83, 1604.17) * mm, "end": v(350.3, 1594.64) * mm});
            skLineSegment(sketch, "E42.0", {"start": v(359.83, 1895.48) * mm, "end": v(359.83, 1604.17) * mm});
            skLineSegment(sketch, "E43.0", {"start": v(350.3, 1594.64) * mm, "end": v(350.3, 1905) * mm});
            skLineSegment(sketch, "E44.0", {"start": v(359.83, 1895.48) * mm, "end": v(350.3, 1905) * mm});
            skLineSegment(sketch, "E45.0", {"start": v(331.26, 1895.47) * mm, "end": v(340.78, 1905) * mm});
            skLineSegment(sketch, "E46.0", {"start": v(340.78, 1594.64) * mm, "end": v(340.78, 1905) * mm});
            skLineSegment(sketch, "E47.0", {"start": v(331.26, 1604.17) * mm, "end": v(340.78, 1594.64) * mm});
            skLineSegment(sketch, "E48.0", {"start": v(331.26, 1895.48) * mm, "end": v(331.26, 1604.17) * mm});
            skLineSegment(sketch, "E49.0", {"start": v(136.52, 1895.48) * mm, "end": v(127, 1905) * mm});
            skLineSegment(sketch, "E50.0", {"start": v(136.52, 1895.48) * mm, "end": v(136.52, 1604.17) * mm});
            skLineSegment(sketch, "E51.0", {"start": v(127, 1594.64) * mm, "end": v(127, 1905) * mm});
            skLineSegment(sketch, "E52.0", {"start": v(136.52, 1604.17) * mm, "end": v(127, 1594.64) * mm});
            skLineSegment(sketch, "E53.0", {"start": v(787.4, 1274.76) * mm, "end": v(787.4, 1585.12) * mm});
            skLineSegment(sketch, "E54.0", {"start": v(777.88, 1575.6) * mm, "end": v(777.88, 1284.29) * mm});
            skLineSegment(sketch, "E55.0", {"start": v(777.88, 1284.29) * mm, "end": v(787.4, 1274.76) * mm});
            skLineSegment(sketch, "E56.0", {"start": v(777.87, 1575.6) * mm, "end": v(787.4, 1585.12) * mm});
            skLineSegment(sketch, "E57.0", {"start": v(583.14, 1575.6) * mm, "end": v(573.62, 1585.12) * mm});
            skLineSegment(sketch, "E58.0", {"start": v(573.62, 1274.76) * mm, "end": v(573.62, 1585.12) * mm});
            skLineSegment(sketch, "E59.0", {"start": v(583.14, 1575.6) * mm, "end": v(583.14, 1284.29) * mm});
            skLineSegment(sketch, "E60.0", {"start": v(583.14, 1284.29) * mm, "end": v(573.62, 1274.76) * mm});
            skLineSegment(sketch, "E61.0", {"start": v(554.57, 1284.29) * mm, "end": v(564.1, 1274.76) * mm});
            skLineSegment(sketch, "E62.0", {"start": v(564.1, 1274.76) * mm, "end": v(564.1, 1585.12) * mm});
            skLineSegment(sketch, "E63.0", {"start": v(554.57, 1575.6) * mm, "end": v(554.57, 1284.29) * mm});
            skLineSegment(sketch, "E64.0", {"start": v(554.57, 1575.6) * mm, "end": v(564.1, 1585.12) * mm});
            skLineSegment(sketch, "E65.0", {"start": v(359.83, 1575.6) * mm, "end": v(350.3, 1585.12) * mm});
            skLineSegment(sketch, "E66.0", {"start": v(359.83, 1575.6) * mm, "end": v(359.83, 1284.29) * mm});
            skLineSegment(sketch, "E67.0", {"start": v(350.3, 1274.76) * mm, "end": v(350.3, 1585.12) * mm});
            skLineSegment(sketch, "E68.0", {"start": v(359.83, 1284.29) * mm, "end": v(350.3, 1274.76) * mm});
            skLineSegment(sketch, "E69.0", {"start": v(331.26, 1284.29) * mm, "end": v(340.78, 1274.76) * mm});
            skLineSegment(sketch, "E70.0", {"start": v(340.78, 1274.76) * mm, "end": v(340.78, 1585.12) * mm});
            skLineSegment(sketch, "E71.0", {"start": v(331.26, 1575.6) * mm, "end": v(331.26, 1284.29) * mm});
            skLineSegment(sketch, "E72.0", {"start": v(331.26, 1575.6) * mm, "end": v(340.78, 1585.12) * mm});
            skLineSegment(sketch, "E73.0", {"start": v(136.52, 1575.6) * mm, "end": v(127, 1585.12) * mm});
            skLineSegment(sketch, "E74.0", {"start": v(136.52, 1575.6) * mm, "end": v(136.52, 1284.29) * mm});
            skLineSegment(sketch, "E75.0", {"start": v(127, 1274.76) * mm, "end": v(127, 1585.12) * mm});
            skLineSegment(sketch, "E76.0", {"start": v(136.52, 1284.29) * mm, "end": v(127, 1274.76) * mm});
            skLineSegment(sketch, "E77.0", {"start": v(777.88, 964.4) * mm, "end": v(787.4, 954.88) * mm});
            skLineSegment(sketch, "E78.0", {"start": v(777.88, 1255.71) * mm, "end": v(777.88, 964.4) * mm});
            skLineSegment(sketch, "E79.0", {"start": v(787.4, 954.88) * mm, "end": v(787.4, 1265.24) * mm});
            skLineSegment(sketch, "E80.0", {"start": v(777.87, 1255.71) * mm, "end": v(787.4, 1265.24) * mm});
            skLineSegment(sketch, "E81.0", {"start": v(583.14, 1255.71) * mm, "end": v(573.62, 1265.24) * mm});
            skLineSegment(sketch, "E82.0", {"start": v(583.14, 1255.71) * mm, "end": v(583.14, 964.4) * mm});
            skLineSegment(sketch, "E83.0", {"start": v(573.62, 954.88) * mm, "end": v(573.62, 1265.24) * mm});
            skLineSegment(sketch, "E84.0", {"start": v(583.14, 964.4) * mm, "end": v(573.62, 954.88) * mm});
            skLineSegment(sketch, "E85.0", {"start": v(554.57, 964.4) * mm, "end": v(564.1, 954.88) * mm});
            skLineSegment(sketch, "E86.0", {"start": v(554.57, 1255.71) * mm, "end": v(554.57, 964.4) * mm});
            skLineSegment(sketch, "E87.0", {"start": v(564.1, 954.88) * mm, "end": v(564.1, 1265.24) * mm});
            skLineSegment(sketch, "E88.0", {"start": v(554.57, 1255.71) * mm, "end": v(564.1, 1265.24) * mm});
            skLineSegment(sketch, "E89.0", {"start": v(359.83, 1255.71) * mm, "end": v(350.3, 1265.24) * mm});
            skLineSegment(sketch, "E90.0", {"start": v(359.83, 1255.71) * mm, "end": v(359.83, 964.4) * mm});
            skLineSegment(sketch, "E91.0", {"start": v(350.3, 954.88) * mm, "end": v(350.3, 1265.24) * mm});
            skLineSegment(sketch, "E92.0", {"start": v(359.83, 964.4) * mm, "end": v(350.3, 954.88) * mm});
            skLineSegment(sketch, "E93.0.0", {"start": v(340.78, 1265.24) * mm, "end": v(331.26, 1255.71) * mm});
            skLineSegment(sketch, "E93.0.1", {"start": v(331.26, 1255.71) * mm, "end": v(331.26, 964.4) * mm});
            skLineSegment(sketch, "E93.0.2", {"start": v(331.26, 964.4) * mm, "end": v(340.78, 954.88) * mm});
            skLineSegment(sketch, "E93.0.3", {"start": v(340.78, 954.88) * mm, "end": v(340.78, 1265.24) * mm});
            skLineSegment(sketch, "E94.0.0", {"start": v(127, 1265.24) * mm, "end": v(127, 954.88) * mm});
            skLineSegment(sketch, "E94.0.1", {"start": v(127, 954.88) * mm, "end": v(136.52, 964.4) * mm});
            skLineSegment(sketch, "E94.0.2", {"start": v(136.52, 964.4) * mm, "end": v(136.52, 1255.71) * mm});
            skLineSegment(sketch, "E94.0.3", {"start": v(136.52, 1255.71) * mm, "end": v(127, 1265.24) * mm});
            skLineSegment(sketch, "E95.0.0", {"start": v(777.88, 644.52) * mm, "end": v(787.4, 635) * mm});
            skLineSegment(sketch, "E95.0.1", {"start": v(787.4, 635) * mm, "end": v(787.4, 945.36) * mm});
            skLineSegment(sketch, "E95.0.2", {"start": v(787.4, 945.36) * mm, "end": v(777.88, 935.83) * mm});
            skLineSegment(sketch, "E95.0.3", {"start": v(777.88, 935.83) * mm, "end": v(777.88, 644.53) * mm});
            skLineSegment(sketch, "E96.0.0", {"start": v(573.62, 945.36) * mm, "end": v(573.62, 635) * mm});
            skLineSegment(sketch, "E96.0.1", {"start": v(573.62, 635) * mm, "end": v(583.14, 644.53) * mm});
            skLineSegment(sketch, "E96.0.2", {"start": v(583.14, 644.53) * mm, "end": v(583.14, 935.83) * mm});
            skLineSegment(sketch, "E96.0.3", {"start": v(583.14, 935.83) * mm, "end": v(573.62, 945.36) * mm});
            skLineSegment(sketch, "E97.0.0", {"start": v(564.1, 945.36) * mm, "end": v(554.57, 935.83) * mm});
            skLineSegment(sketch, "E97.0.1", {"start": v(554.57, 935.83) * mm, "end": v(554.57, 644.53) * mm});
            skLineSegment(sketch, "E97.0.2", {"start": v(554.57, 644.52) * mm, "end": v(564.1, 635) * mm});
            skLineSegment(sketch, "E97.0.3", {"start": v(564.1, 635) * mm, "end": v(564.1, 945.36) * mm});
            skLineSegment(sketch, "E98.0.0", {"start": v(350.3, 945.36) * mm, "end": v(350.3, 635) * mm});
            skLineSegment(sketch, "E98.0.1", {"start": v(350.3, 635) * mm, "end": v(359.83, 644.52) * mm});
            skLineSegment(sketch, "E98.0.2", {"start": v(359.83, 644.52) * mm, "end": v(359.83, 935.83) * mm});
            skLineSegment(sketch, "E98.0.3", {"start": v(359.83, 935.83) * mm, "end": v(350.3, 945.36) * mm});
            skLineSegment(sketch, "E99.0.0", {"start": v(340.78, 945.36) * mm, "end": v(331.26, 935.83) * mm});
            skLineSegment(sketch, "E99.0.1", {"start": v(331.26, 935.83) * mm, "end": v(331.26, 644.53) * mm});
            skLineSegment(sketch, "E99.0.2", {"start": v(331.26, 644.52) * mm, "end": v(340.78, 635) * mm});
            skLineSegment(sketch, "E99.0.3", {"start": v(340.78, 635) * mm, "end": v(340.78, 945.36) * mm});
            skLineSegment(sketch, "E100.0.0", {"start": v(127, 945.36) * mm, "end": v(127, 635) * mm});
            skLineSegment(sketch, "E100.0.1", {"start": v(127, 635) * mm, "end": v(136.53, 644.53) * mm});
            skLineSegment(sketch, "E100.0.2", {"start": v(136.52, 644.52) * mm, "end": v(136.52, 935.83) * mm});
            skLineSegment(sketch, "E100.0.3", {"start": v(136.52, 935.83) * mm, "end": v(127, 945.36) * mm});
            skSolve(sketch);
        }
        {
            var Q0;
            Q0=qSketchRegion(id+"F3",true);
            extrude(context, id + "F4", {"entities" : qUnion([Q0]), "operationType" : NewBodyOperationType.ADD, "depth" : 20 * mm, "hasSecondDirection" : true, "secondDirectionOppositeDirection" : true, "secondDirectionDepth" : 20.02 * mm});
        }
        {
            var Q0;
            Q0=qCreatedBy(makeId("Front.planeOp"),FACE);
            var sketch = newSketch(context, id + "F5", { "sketchPlane" : qUnion([Q0])});
            skLineSegment(sketch, "E101.0.0", {"start": v(573.62, 1905) * mm, "end": v(583.14, 1895.48) * mm});
            skLineSegment(sketch, "E101.0.1", {"start": v(583.14, 1895.48) * mm, "end": v(777.88, 1895.48) * mm});
            skLineSegment(sketch, "E101.0.2", {"start": v(777.88, 1895.47) * mm, "end": v(787.4, 1905) * mm});
            skLineSegment(sketch, "E101.0.3", {"start": v(787.4, 1905) * mm, "end": v(573.62, 1905) * mm});
            skLineSegment(sketch, "E102.0.0", {"start": v(350.3, 1905) * mm, "end": v(359.83, 1895.48) * mm});
            skLineSegment(sketch, "E102.0.1", {"start": v(359.83, 1895.48) * mm, "end": v(554.57, 1895.48) * mm});
            skLineSegment(sketch, "E102.0.2", {"start": v(554.57, 1895.47) * mm, "end": v(564.1, 1905) * mm});
            skLineSegment(sketch, "E102.0.3", {"start": v(564.1, 1905) * mm, "end": v(350.3, 1905) * mm});
            skLineSegment(sketch, "E103.0.0", {"start": v(127, 1905) * mm, "end": v(136.52, 1895.48) * mm});
            skLineSegment(sketch, "E103.0.1", {"start": v(136.52, 1895.48) * mm, "end": v(331.26, 1895.48) * mm});
            skLineSegment(sketch, "E103.0.2", {"start": v(331.26, 1895.47) * mm, "end": v(340.78, 1905) * mm});
            skLineSegment(sketch, "E103.0.3", {"start": v(340.78, 1905) * mm, "end": v(127, 1905) * mm});
            skLineSegment(sketch, "E104.0.0", {"start": v(777.88, 1604.17) * mm, "end": v(583.14, 1604.17) * mm});
            skLineSegment(sketch, "E104.0.1", {"start": v(583.14, 1604.17) * mm, "end": v(573.62, 1594.64) * mm});
            skLineSegment(sketch, "E104.0.2", {"start": v(573.62, 1594.64) * mm, "end": v(787.4, 1594.64) * mm});
            skLineSegment(sketch, "E104.0.3", {"start": v(787.4, 1594.64) * mm, "end": v(777.88, 1604.17) * mm});
            skLineSegment(sketch, "E105.0.0", {"start": v(554.57, 1604.17) * mm, "end": v(359.83, 1604.17) * mm});
            skLineSegment(sketch, "E105.0.1", {"start": v(359.83, 1604.17) * mm, "end": v(350.3, 1594.64) * mm});
            skLineSegment(sketch, "E105.0.2", {"start": v(350.3, 1594.64) * mm, "end": v(564.1, 1594.64) * mm});
            skLineSegment(sketch, "E105.0.3", {"start": v(564.1, 1594.64) * mm, "end": v(554.57, 1604.17) * mm});
            skLineSegment(sketch, "E106.0.0", {"start": v(331.26, 1604.17) * mm, "end": v(136.53, 1604.17) * mm});
            skLineSegment(sketch, "E106.0.1", {"start": v(136.52, 1604.17) * mm, "end": v(127, 1594.64) * mm});
            skLineSegment(sketch, "E106.0.2", {"start": v(127, 1594.64) * mm, "end": v(340.78, 1594.64) * mm});
            skLineSegment(sketch, "E106.0.3", {"start": v(340.78, 1594.64) * mm, "end": v(331.26, 1604.17) * mm});
            skLineSegment(sketch, "E107.0.0", {"start": v(573.62, 1585.12) * mm, "end": v(583.14, 1575.6) * mm});
            skLineSegment(sketch, "E107.0.1", {"start": v(583.14, 1575.6) * mm, "end": v(777.88, 1575.6) * mm});
            skLineSegment(sketch, "E107.0.2", {"start": v(777.87, 1575.6) * mm, "end": v(787.4, 1585.12) * mm});
            skLineSegment(sketch, "E107.0.3", {"start": v(787.4, 1585.12) * mm, "end": v(573.62, 1585.12) * mm});
            skLineSegment(sketch, "E108.0.0", {"start": v(350.3, 1585.12) * mm, "end": v(359.83, 1575.6) * mm});
            skLineSegment(sketch, "E108.0.1", {"start": v(359.83, 1575.6) * mm, "end": v(554.57, 1575.6) * mm});
            skLineSegment(sketch, "E108.0.2", {"start": v(554.57, 1575.6) * mm, "end": v(564.1, 1585.12) * mm});
            skLineSegment(sketch, "E108.0.3", {"start": v(564.1, 1585.12) * mm, "end": v(350.3, 1585.12) * mm});
            skLineSegment(sketch, "E109.0.0", {"start": v(127, 1585.12) * mm, "end": v(136.52, 1575.6) * mm});
            skLineSegment(sketch, "E109.0.1", {"start": v(136.53, 1575.6) * mm, "end": v(331.26, 1575.6) * mm});
            skLineSegment(sketch, "E109.0.2", {"start": v(331.26, 1575.6) * mm, "end": v(340.78, 1585.12) * mm});
            skLineSegment(sketch, "E109.0.3", {"start": v(340.78, 1585.12) * mm, "end": v(127, 1585.12) * mm});
            skLineSegment(sketch, "E110.0.0", {"start": v(331.26, 1284.29) * mm, "end": v(136.53, 1284.29) * mm});
            skLineSegment(sketch, "E110.0.1", {"start": v(136.52, 1284.29) * mm, "end": v(127, 1274.76) * mm});
            skLineSegment(sketch, "E110.0.2", {"start": v(127, 1274.76) * mm, "end": v(340.78, 1274.76) * mm});
            skLineSegment(sketch, "E110.0.3", {"start": v(340.78, 1274.76) * mm, "end": v(331.26, 1284.29) * mm});
            skLineSegment(sketch, "E111.0.0", {"start": v(127, 1265.24) * mm, "end": v(136.52, 1255.71) * mm});
            skLineSegment(sketch, "E111.0.1", {"start": v(136.53, 1255.71) * mm, "end": v(331.26, 1255.71) * mm});
            skLineSegment(sketch, "E111.0.2", {"start": v(331.26, 1255.71) * mm, "end": v(340.78, 1265.24) * mm});
            skLineSegment(sketch, "E111.0.3", {"start": v(340.78, 1265.24) * mm, "end": v(127, 1265.24) * mm});
            skLineSegment(sketch, "E112.0.0", {"start": v(350.3, 1265.24) * mm, "end": v(359.83, 1255.71) * mm});
            skLineSegment(sketch, "E112.0.1", {"start": v(359.83, 1255.71) * mm, "end": v(554.57, 1255.71) * mm});
            skLineSegment(sketch, "E112.0.2", {"start": v(554.57, 1255.71) * mm, "end": v(564.1, 1265.24) * mm});
            skLineSegment(sketch, "E112.0.3", {"start": v(564.1, 1265.24) * mm, "end": v(350.3, 1265.24) * mm});
            skLineSegment(sketch, "E113.0.0", {"start": v(554.57, 1284.29) * mm, "end": v(359.83, 1284.29) * mm});
            skLineSegment(sketch, "E113.0.1", {"start": v(359.83, 1284.29) * mm, "end": v(350.3, 1274.76) * mm});
            skLineSegment(sketch, "E113.0.2", {"start": v(350.3, 1274.76) * mm, "end": v(564.1, 1274.76) * mm});
            skLineSegment(sketch, "E113.0.3", {"start": v(564.1, 1274.76) * mm, "end": v(554.57, 1284.29) * mm});
            skLineSegment(sketch, "E114.0.0", {"start": v(777.88, 1284.29) * mm, "end": v(583.14, 1284.29) * mm});
            skLineSegment(sketch, "E114.0.1", {"start": v(583.14, 1284.29) * mm, "end": v(573.62, 1274.76) * mm});
            skLineSegment(sketch, "E114.0.2", {"start": v(573.62, 1274.76) * mm, "end": v(787.4, 1274.76) * mm});
            skLineSegment(sketch, "E114.0.3", {"start": v(787.4, 1274.76) * mm, "end": v(777.88, 1284.29) * mm});
            skLineSegment(sketch, "E115.0.0", {"start": v(573.62, 1265.24) * mm, "end": v(583.14, 1255.71) * mm});
            skLineSegment(sketch, "E115.0.1", {"start": v(583.14, 1255.71) * mm, "end": v(777.88, 1255.71) * mm});
            skLineSegment(sketch, "E115.0.2", {"start": v(777.87, 1255.71) * mm, "end": v(787.4, 1265.24) * mm});
            skLineSegment(sketch, "E115.0.3", {"start": v(787.4, 1265.24) * mm, "end": v(573.62, 1265.24) * mm});
            skLineSegment(sketch, "E116.0.0", {"start": v(777.88, 964.4) * mm, "end": v(583.14, 964.4) * mm});
            skLineSegment(sketch, "E116.0.1", {"start": v(583.14, 964.4) * mm, "end": v(573.62, 954.88) * mm});
            skLineSegment(sketch, "E116.0.2", {"start": v(573.62, 954.88) * mm, "end": v(787.4, 954.88) * mm});
            skLineSegment(sketch, "E116.0.3", {"start": v(787.4, 954.88) * mm, "end": v(777.88, 964.4) * mm});
            skLineSegment(sketch, "E117.0.0", {"start": v(777.88, 935.83) * mm, "end": v(787.4, 945.36) * mm});
            skLineSegment(sketch, "E117.0.1", {"start": v(787.4, 945.36) * mm, "end": v(573.62, 945.36) * mm});
            skLineSegment(sketch, "E117.0.2", {"start": v(573.62, 945.36) * mm, "end": v(583.14, 935.83) * mm});
            skLineSegment(sketch, "E117.0.3", {"start": v(583.14, 935.83) * mm, "end": v(777.88, 935.83) * mm});
            skLineSegment(sketch, "E118.0.0", {"start": v(350.3, 945.36) * mm, "end": v(359.83, 935.83) * mm});
            skLineSegment(sketch, "E118.0.1", {"start": v(359.83, 935.83) * mm, "end": v(554.57, 935.83) * mm});
            skLineSegment(sketch, "E118.0.2", {"start": v(554.57, 935.83) * mm, "end": v(564.1, 945.36) * mm});
            skLineSegment(sketch, "E118.0.3", {"start": v(564.1, 945.36) * mm, "end": v(350.3, 945.36) * mm});
            skLineSegment(sketch, "E119.0.0", {"start": v(554.57, 964.4) * mm, "end": v(359.83, 964.4) * mm});
            skLineSegment(sketch, "E119.0.1", {"start": v(359.83, 964.4) * mm, "end": v(350.3, 954.88) * mm});
            skLineSegment(sketch, "E119.0.2", {"start": v(350.3, 954.88) * mm, "end": v(564.1, 954.88) * mm});
            skLineSegment(sketch, "E119.0.3", {"start": v(564.1, 954.88) * mm, "end": v(554.57, 964.4) * mm});
            skLineSegment(sketch, "E120.0.0", {"start": v(127, 945.36) * mm, "end": v(136.52, 935.83) * mm});
            skLineSegment(sketch, "E120.0.1", {"start": v(136.53, 935.83) * mm, "end": v(331.26, 935.83) * mm});
            skLineSegment(sketch, "E120.0.2", {"start": v(331.26, 935.83) * mm, "end": v(340.78, 945.36) * mm});
            skLineSegment(sketch, "E120.0.3", {"start": v(340.78, 945.36) * mm, "end": v(127, 945.36) * mm});
            skLineSegment(sketch, "E121.0.0", {"start": v(331.26, 964.4) * mm, "end": v(136.53, 964.4) * mm});
            skLineSegment(sketch, "E121.0.1", {"start": v(136.52, 964.4) * mm, "end": v(127, 954.88) * mm});
            skLineSegment(sketch, "E121.0.2", {"start": v(127, 954.88) * mm, "end": v(340.78, 954.88) * mm});
            skLineSegment(sketch, "E121.0.3", {"start": v(340.78, 954.88) * mm, "end": v(331.26, 964.4) * mm});
            skLineSegment(sketch, "E122.0.0", {"start": v(573.62, 635) * mm, "end": v(787.4, 635) * mm});
            skLineSegment(sketch, "E122.0.1", {"start": v(787.4, 635) * mm, "end": v(777.88, 644.52) * mm});
            skLineSegment(sketch, "E122.0.2", {"start": v(777.88, 644.53) * mm, "end": v(583.14, 644.53) * mm});
            skLineSegment(sketch, "E122.0.3", {"start": v(583.14, 644.53) * mm, "end": v(573.62, 635) * mm});
            skLineSegment(sketch, "E123.0.0", {"start": v(554.57, 644.53) * mm, "end": v(359.83, 644.53) * mm});
            skLineSegment(sketch, "E123.0.1", {"start": v(359.83, 644.52) * mm, "end": v(350.3, 635) * mm});
            skLineSegment(sketch, "E123.0.2", {"start": v(350.3, 635) * mm, "end": v(564.1, 635) * mm});
            skLineSegment(sketch, "E123.0.3", {"start": v(564.1, 635) * mm, "end": v(554.57, 644.52) * mm});
            skLineSegment(sketch, "E124.0.0", {"start": v(331.26, 644.53) * mm, "end": v(136.53, 644.53) * mm});
            skLineSegment(sketch, "E124.0.1", {"start": v(136.53, 644.53) * mm, "end": v(127, 635) * mm});
            skLineSegment(sketch, "E124.0.2", {"start": v(127, 635) * mm, "end": v(340.78, 635) * mm});
            skLineSegment(sketch, "E124.0.3", {"start": v(340.78, 635) * mm, "end": v(331.26, 644.52) * mm});
            skSolve(sketch);
        }
        {
            var Q0;
            Q0=qSketchRegion(id+"F5",true);
            extrude(context, id + "F6", {"entities" : qUnion([Q0]), "operationType" : NewBodyOperationType.ADD, "depth" : 19.05 * mm, "hasSecondDirection" : true, "secondDirectionOppositeDirection" : true, "secondDirectionDepth" : 19.05 * mm});
        }
        {
            var Q0;
            Q0=qCreatedBy(makeId("Front.planeOp"),FACE);
            var sketch = newSketch(context, id + "F7", { "sketchPlane" : qUnion([Q0])});
            skLineSegment(sketch, "E125.0.0", {"start": v(583.14, 1895.47) * mm, "end": v(583.14, 1604.17) * mm});
            skLineSegment(sketch, "E125.0.1", {"start": v(583.14, 1604.17) * mm, "end": v(777.88, 1604.17) * mm});
            skLineSegment(sketch, "E125.0.2", {"start": v(777.88, 1604.17) * mm, "end": v(777.88, 1895.47) * mm});
            skLineSegment(sketch, "E125.0.3", {"start": v(777.88, 1895.48) * mm, "end": v(583.14, 1895.48) * mm});
            skLineSegment(sketch, "E126.0.0", {"start": v(359.83, 1895.47) * mm, "end": v(359.83, 1604.17) * mm});
            skLineSegment(sketch, "E126.0.1", {"start": v(359.83, 1604.17) * mm, "end": v(554.57, 1604.17) * mm});
            skLineSegment(sketch, "E126.0.2", {"start": v(554.57, 1604.17) * mm, "end": v(554.57, 1895.47) * mm});
            skLineSegment(sketch, "E126.0.3", {"start": v(554.57, 1895.48) * mm, "end": v(359.83, 1895.48) * mm});
            skLineSegment(sketch, "E127.0.0", {"start": v(136.52, 1895.48) * mm, "end": v(136.52, 1604.17) * mm});
            skLineSegment(sketch, "E127.0.1", {"start": v(136.53, 1604.17) * mm, "end": v(331.26, 1604.17) * mm});
            skLineSegment(sketch, "E127.0.2", {"start": v(331.26, 1604.17) * mm, "end": v(331.26, 1895.47) * mm});
            skLineSegment(sketch, "E127.0.3", {"start": v(331.26, 1895.48) * mm, "end": v(136.52, 1895.48) * mm});
            skLineSegment(sketch, "E128.0.0", {"start": v(583.14, 1575.6) * mm, "end": v(583.14, 1284.29) * mm});
            skLineSegment(sketch, "E128.0.1", {"start": v(583.14, 1284.29) * mm, "end": v(777.88, 1284.29) * mm});
            skLineSegment(sketch, "E128.0.2", {"start": v(777.88, 1284.29) * mm, "end": v(777.88, 1575.6) * mm});
            skLineSegment(sketch, "E128.0.3", {"start": v(777.88, 1575.6) * mm, "end": v(583.14, 1575.6) * mm});
            skLineSegment(sketch, "E129.0.0", {"start": v(359.83, 1575.6) * mm, "end": v(359.83, 1284.29) * mm});
            skLineSegment(sketch, "E129.0.1", {"start": v(359.83, 1284.29) * mm, "end": v(554.57, 1284.29) * mm});
            skLineSegment(sketch, "E129.0.2", {"start": v(554.57, 1284.29) * mm, "end": v(554.57, 1575.6) * mm});
            skLineSegment(sketch, "E129.0.3", {"start": v(554.57, 1575.6) * mm, "end": v(359.83, 1575.6) * mm});
            skLineSegment(sketch, "E130.0.0", {"start": v(136.52, 1575.6) * mm, "end": v(136.52, 1284.29) * mm});
            skLineSegment(sketch, "E130.0.1", {"start": v(136.53, 1284.29) * mm, "end": v(331.26, 1284.29) * mm});
            skLineSegment(sketch, "E130.0.2", {"start": v(331.26, 1284.29) * mm, "end": v(331.26, 1575.6) * mm});
            skLineSegment(sketch, "E130.0.3", {"start": v(331.26, 1575.6) * mm, "end": v(136.53, 1575.6) * mm});
            skLineSegment(sketch, "E131.0.0", {"start": v(583.14, 1255.71) * mm, "end": v(583.14, 964.4) * mm});
            skLineSegment(sketch, "E131.0.1", {"start": v(583.14, 964.4) * mm, "end": v(777.88, 964.4) * mm});
            skLineSegment(sketch, "E131.0.2", {"start": v(777.88, 964.4) * mm, "end": v(777.88, 1255.71) * mm});
            skLineSegment(sketch, "E131.0.3", {"start": v(777.88, 1255.71) * mm, "end": v(583.14, 1255.71) * mm});
            skLineSegment(sketch, "E132.0.0", {"start": v(359.83, 1255.71) * mm, "end": v(359.83, 964.4) * mm});
            skLineSegment(sketch, "E132.0.1", {"start": v(359.83, 964.4) * mm, "end": v(554.57, 964.4) * mm});
            skLineSegment(sketch, "E132.0.2", {"start": v(554.57, 964.4) * mm, "end": v(554.57, 1255.71) * mm});
            skLineSegment(sketch, "E132.0.3", {"start": v(554.57, 1255.71) * mm, "end": v(359.83, 1255.71) * mm});
            skLineSegment(sketch, "E133.0.0", {"start": v(136.52, 1255.71) * mm, "end": v(136.52, 964.4) * mm});
            skLineSegment(sketch, "E133.0.1", {"start": v(136.53, 964.4) * mm, "end": v(331.26, 964.4) * mm});
            skLineSegment(sketch, "E133.0.2", {"start": v(331.26, 964.4) * mm, "end": v(331.26, 1255.71) * mm});
            skLineSegment(sketch, "E133.0.3", {"start": v(331.26, 1255.71) * mm, "end": v(136.53, 1255.71) * mm});
            skLineSegment(sketch, "E134.0.0", {"start": v(136.52, 935.83) * mm, "end": v(136.52, 644.52) * mm});
            skLineSegment(sketch, "E134.0.1", {"start": v(136.53, 644.53) * mm, "end": v(331.26, 644.53) * mm});
            skLineSegment(sketch, "E134.0.2", {"start": v(331.26, 644.53) * mm, "end": v(331.26, 935.83) * mm});
            skLineSegment(sketch, "E134.0.3", {"start": v(331.26, 935.83) * mm, "end": v(136.53, 935.83) * mm});
            skLineSegment(sketch, "E135.0.0", {"start": v(359.83, 935.83) * mm, "end": v(359.83, 644.52) * mm});
            skLineSegment(sketch, "E135.0.1", {"start": v(359.83, 644.53) * mm, "end": v(554.57, 644.53) * mm});
            skLineSegment(sketch, "E135.0.2", {"start": v(554.57, 644.53) * mm, "end": v(554.57, 935.83) * mm});
            skLineSegment(sketch, "E135.0.3", {"start": v(554.57, 935.83) * mm, "end": v(359.83, 935.83) * mm});
            skLineSegment(sketch, "E136.0.0", {"start": v(777.88, 935.83) * mm, "end": v(583.14, 935.83) * mm});
            skLineSegment(sketch, "E136.0.1", {"start": v(583.14, 935.83) * mm, "end": v(583.14, 644.53) * mm});
            skLineSegment(sketch, "E136.0.2", {"start": v(583.14, 644.53) * mm, "end": v(777.88, 644.53) * mm});
            skLineSegment(sketch, "E136.0.3", {"start": v(777.88, 644.53) * mm, "end": v(777.88, 935.83) * mm});
            skSolve(sketch);
        }
        {
            var Q0;
            Q0=qSketchRegion(id+"F7",true);
            extrude(context, id + "F8", {"entities" : qUnion([Q0]), "operationType" : NewBodyOperationType.ADD, "depth" : 3.17 * mm, "hasSecondDirection" : true, "secondDirectionOppositeDirection" : true, "secondDirectionDepth" : 3.17 * mm});
        }
        {
            var Q0;
            Q0=qCreatedBy(makeId("Front.planeOp"),FACE);
            var sketch = newSketch(context, id + "F9", { "sketchPlane" : qUnion([Q0])});
            skLineSegment(sketch, "E137.0", {"start": v(701.75, 1810.54) * mm, "end": v(619, 1722.43) * mm});
            skLineSegment(sketch, "E138.0", {"start": v(621.24, 1686.72) * mm, "end": v(739.77, 1812.92) * mm});
            skLineSegment(sketch, "E139.0", {"start": v(739.77, 1774.82) * mm, "end": v(657.03, 1686.72) * mm});
            skLineSegment(sketch, "E140.0", {"start": v(516.47, 1774.82) * mm, "end": v(433.72, 1686.72) * mm});
            skLineSegment(sketch, "E141.0", {"start": v(397.93, 1686.72) * mm, "end": v(516.47, 1812.92) * mm});
            skLineSegment(sketch, "E142.0", {"start": v(478.44, 1810.54) * mm, "end": v(395.7, 1722.43) * mm});
            skLineSegment(sketch, "E143.0", {"start": v(293.16, 1774.82) * mm, "end": v(210.4, 1686.72) * mm});
            skLineSegment(sketch, "E144.0", {"start": v(174.63, 1686.72) * mm, "end": v(293.16, 1812.92) * mm});
            skLineSegment(sketch, "E145.0", {"start": v(255.13, 1810.54) * mm, "end": v(172.38, 1722.43) * mm});
            skLineSegment(sketch, "E146.0", {"start": v(739.77, 1454.94) * mm, "end": v(657.03, 1366.84) * mm});
            skLineSegment(sketch, "E147.0", {"start": v(621.24, 1366.84) * mm, "end": v(739.78, 1493.04) * mm});
            skLineSegment(sketch, "E148.0", {"start": v(701.75, 1490.66) * mm, "end": v(619, 1402.55) * mm});
            skLineSegment(sketch, "E149.0", {"start": v(516.47, 1454.94) * mm, "end": v(433.72, 1366.84) * mm});
            skLineSegment(sketch, "E150.0", {"start": v(397.93, 1366.84) * mm, "end": v(516.47, 1493.04) * mm});
            skLineSegment(sketch, "E151.0", {"start": v(478.44, 1490.66) * mm, "end": v(395.7, 1402.55) * mm});
            skLineSegment(sketch, "E152.0", {"start": v(293.16, 1454.94) * mm, "end": v(210.4, 1366.84) * mm});
            skLineSegment(sketch, "E153.0", {"start": v(174.63, 1366.84) * mm, "end": v(293.16, 1493.04) * mm});
            skLineSegment(sketch, "E154.0", {"start": v(255.13, 1490.66) * mm, "end": v(172.38, 1402.55) * mm});
            skLineSegment(sketch, "E155.0", {"start": v(701.75, 1170.78) * mm, "end": v(619, 1082.67) * mm});
            skLineSegment(sketch, "E156.0", {"start": v(621.24, 1046.96) * mm, "end": v(739.78, 1173.16) * mm});
            skLineSegment(sketch, "E157.0", {"start": v(739.78, 1135.06) * mm, "end": v(657.03, 1046.96) * mm});
            skLineSegment(sketch, "E158.0", {"start": v(516.47, 1135.06) * mm, "end": v(433.72, 1046.96) * mm});
            skLineSegment(sketch, "E159.0", {"start": v(397.93, 1046.96) * mm, "end": v(516.47, 1173.16) * mm});
            skLineSegment(sketch, "E160.0", {"start": v(478.44, 1170.78) * mm, "end": v(395.7, 1082.67) * mm});
            skLineSegment(sketch, "E161.0", {"start": v(293.16, 1135.06) * mm, "end": v(210.4, 1046.96) * mm});
            skLineSegment(sketch, "E162.0", {"start": v(174.63, 1046.96) * mm, "end": v(293.16, 1173.16) * mm});
            skLineSegment(sketch, "E163.0", {"start": v(255.13, 1170.78) * mm, "end": v(172.38, 1082.67) * mm});
            skLineSegment(sketch, "E164.0", {"start": v(701.75, 850.9) * mm, "end": v(619, 762.79) * mm});
            skLineSegment(sketch, "E165.0", {"start": v(621.24, 727.08) * mm, "end": v(739.78, 853.28) * mm});
            skLineSegment(sketch, "E166.0", {"start": v(739.78, 815.18) * mm, "end": v(657.03, 727.08) * mm});
            skLineSegment(sketch, "E167.0", {"start": v(516.47, 815.18) * mm, "end": v(433.72, 727.08) * mm});
            skLineSegment(sketch, "E168.0", {"start": v(397.93, 727.08) * mm, "end": v(516.47, 853.28) * mm});
            skLineSegment(sketch, "E169.0", {"start": v(478.44, 850.9) * mm, "end": v(395.7, 762.79) * mm});
            skLineSegment(sketch, "E170.0", {"start": v(293.16, 815.18) * mm, "end": v(210.4, 727.08) * mm});
            skLineSegment(sketch, "E171.0", {"start": v(174.63, 727.08) * mm, "end": v(293.16, 853.28) * mm});
            skLineSegment(sketch, "E172.0", {"start": v(255.13, 850.9) * mm, "end": v(172.38, 762.79) * mm});
            skArc(sketch, "E173.0.startCap", {"start": v(699.44, 1812.71) * mm, "mid": v(703.92, 1812.85) * mm, "end": v(704.06, 1808.36) * mm});
            skArc(sketch, "E173.0.endCap", {"start": v(621.31, 1720.26) * mm, "mid": v(616.83, 1720.12) * mm, "end": v(616.69, 1724.6) * mm});
            skLineSegment(sketch, "E173.0.left", {"start": v(704.06, 1808.36) * mm, "end": v(621.31, 1720.26) * mm});
            skLineSegment(sketch, "E173.0.right", {"start": v(699.44, 1812.71) * mm, "end": v(616.69, 1724.6) * mm});
            skArc(sketch, "E173.1.startCap", {"start": v(514.15, 1777) * mm, "mid": v(518.64, 1777.14) * mm, "end": v(518.78, 1772.65) * mm});
            skArc(sketch, "E173.1.endCap", {"start": v(436.03, 1684.55) * mm, "mid": v(431.54, 1684.4) * mm, "end": v(431.4, 1688.9) * mm});
            skLineSegment(sketch, "E173.1.left", {"start": v(518.78, 1772.65) * mm, "end": v(436.03, 1684.55) * mm});
            skLineSegment(sketch, "E173.1.right", {"start": v(514.15, 1777) * mm, "end": v(431.4, 1688.9) * mm});
            skArc(sketch, "E173.2.startCap", {"start": v(400.25, 1684.55) * mm, "mid": v(395.76, 1684.4) * mm, "end": v(395.62, 1688.9) * mm});
            skArc(sketch, "E173.2.endCap", {"start": v(514.15, 1815.1) * mm, "mid": v(518.64, 1815.24) * mm, "end": v(518.78, 1810.75) * mm});
            skLineSegment(sketch, "E173.2.left", {"start": v(395.62, 1688.9) * mm, "end": v(514.15, 1815.1) * mm});
            skLineSegment(sketch, "E173.2.right", {"start": v(400.25, 1684.55) * mm, "end": v(518.78, 1810.75) * mm});
            skArc(sketch, "E173.3.startCap", {"start": v(514.15, 817.35) * mm, "mid": v(518.64, 817.5) * mm, "end": v(518.78, 813) * mm});
            skArc(sketch, "E173.3.endCap", {"start": v(436.03, 724.9) * mm, "mid": v(431.54, 724.76) * mm, "end": v(431.4, 729.25) * mm});
            skLineSegment(sketch, "E173.3.left", {"start": v(518.78, 813) * mm, "end": v(436.03, 724.9) * mm});
            skLineSegment(sketch, "E173.3.right", {"start": v(514.15, 817.35) * mm, "end": v(431.4, 729.25) * mm});
            skArc(sketch, "E173.4.startCap", {"start": v(737.46, 1777) * mm, "mid": v(741.95, 1777.14) * mm, "end": v(742.09, 1772.65) * mm});
            skArc(sketch, "E173.4.endCap", {"start": v(659.34, 1684.55) * mm, "mid": v(654.85, 1684.4) * mm, "end": v(654.71, 1688.9) * mm});
            skLineSegment(sketch, "E173.4.left", {"start": v(742.09, 1772.65) * mm, "end": v(659.34, 1684.55) * mm});
            skLineSegment(sketch, "E173.4.right", {"start": v(737.46, 1777) * mm, "end": v(654.71, 1688.9) * mm});
            skArc(sketch, "E173.5.startCap", {"start": v(699.44, 853.07) * mm, "mid": v(703.92, 853.2) * mm, "end": v(704.06, 848.72) * mm});
            skArc(sketch, "E173.5.endCap", {"start": v(621.31, 760.61) * mm, "mid": v(616.83, 760.47) * mm, "end": v(616.69, 764.96) * mm});
            skLineSegment(sketch, "E173.5.left", {"start": v(704.06, 848.72) * mm, "end": v(621.31, 760.61) * mm});
            skLineSegment(sketch, "E173.5.right", {"start": v(699.44, 853.07) * mm, "end": v(616.69, 764.96) * mm});
            skArc(sketch, "E173.6.startCap", {"start": v(623.56, 1684.55) * mm, "mid": v(619.07, 1684.4) * mm, "end": v(618.93, 1688.9) * mm});
            skArc(sketch, "E173.6.endCap", {"start": v(737.46, 1815.1) * mm, "mid": v(741.95, 1815.24) * mm, "end": v(742.09, 1810.75) * mm});
            skLineSegment(sketch, "E173.6.left", {"start": v(618.93, 1688.9) * mm, "end": v(737.46, 1815.1) * mm});
            skLineSegment(sketch, "E173.6.right", {"start": v(623.56, 1684.55) * mm, "end": v(742.09, 1810.75) * mm});
            skArc(sketch, "E173.7.startCap", {"start": v(176.94, 1364.66) * mm, "mid": v(172.45, 1364.52) * mm, "end": v(172.31, 1369.01) * mm});
            skArc(sketch, "E173.7.endCap", {"start": v(290.84, 1495.22) * mm, "mid": v(295.33, 1495.36) * mm, "end": v(295.47, 1490.87) * mm});
            skLineSegment(sketch, "E173.7.left", {"start": v(172.31, 1369.01) * mm, "end": v(290.84, 1495.22) * mm});
            skLineSegment(sketch, "E173.7.right", {"start": v(176.94, 1364.66) * mm, "end": v(295.47, 1490.87) * mm});
            skArc(sketch, "E173.8.startCap", {"start": v(476.13, 1812.71) * mm, "mid": v(480.62, 1812.85) * mm, "end": v(480.76, 1808.36) * mm});
            skArc(sketch, "E173.8.endCap", {"start": v(398, 1720.26) * mm, "mid": v(393.52, 1720.12) * mm, "end": v(393.38, 1724.6) * mm});
            skLineSegment(sketch, "E173.8.left", {"start": v(480.76, 1808.36) * mm, "end": v(398, 1720.26) * mm});
            skLineSegment(sketch, "E173.8.right", {"start": v(476.13, 1812.71) * mm, "end": v(393.38, 1724.6) * mm});
            skArc(sketch, "E173.9.startCap", {"start": v(290.84, 1777) * mm, "mid": v(295.33, 1777.14) * mm, "end": v(295.47, 1772.65) * mm});
            skArc(sketch, "E173.9.endCap", {"start": v(212.72, 1684.55) * mm, "mid": v(208.24, 1684.4) * mm, "end": v(208.1, 1688.9) * mm});
            skLineSegment(sketch, "E173.9.left", {"start": v(295.47, 1772.65) * mm, "end": v(212.72, 1684.55) * mm});
            skLineSegment(sketch, "E173.9.right", {"start": v(290.84, 1777) * mm, "end": v(208.1, 1688.9) * mm});
            skArc(sketch, "E173.10.startCap", {"start": v(476.13, 853.07) * mm, "mid": v(480.62, 853.2) * mm, "end": v(480.76, 848.72) * mm});
            skArc(sketch, "E173.10.endCap", {"start": v(398, 760.61) * mm, "mid": v(393.52, 760.47) * mm, "end": v(393.38, 764.96) * mm});
            skLineSegment(sketch, "E173.10.left", {"start": v(480.76, 848.72) * mm, "end": v(398, 760.61) * mm});
            skLineSegment(sketch, "E173.10.right", {"start": v(476.13, 853.07) * mm, "end": v(393.38, 764.96) * mm});
            skArc(sketch, "E173.11.startCap", {"start": v(290.84, 1457.12) * mm, "mid": v(295.33, 1457.26) * mm, "end": v(295.47, 1452.77) * mm});
            skArc(sketch, "E173.11.endCap", {"start": v(212.72, 1364.66) * mm, "mid": v(208.24, 1364.52) * mm, "end": v(208.1, 1369.01) * mm});
            skLineSegment(sketch, "E173.11.left", {"start": v(295.47, 1452.77) * mm, "end": v(212.72, 1364.66) * mm});
            skLineSegment(sketch, "E173.11.right", {"start": v(290.84, 1457.12) * mm, "end": v(208.1, 1369.01) * mm});
            skArc(sketch, "E173.12.startCap", {"start": v(176.94, 1684.55) * mm, "mid": v(172.45, 1684.4) * mm, "end": v(172.31, 1688.9) * mm});
            skArc(sketch, "E173.12.endCap", {"start": v(290.84, 1815.1) * mm, "mid": v(295.33, 1815.24) * mm, "end": v(295.47, 1810.75) * mm});
            skLineSegment(sketch, "E173.12.left", {"start": v(172.31, 1688.9) * mm, "end": v(290.84, 1815.1) * mm});
            skLineSegment(sketch, "E173.12.right", {"start": v(176.94, 1684.55) * mm, "end": v(295.47, 1810.75) * mm});
            skArc(sketch, "E173.13.startCap", {"start": v(400.25, 724.9) * mm, "mid": v(395.76, 724.76) * mm, "end": v(395.62, 729.25) * mm});
            skArc(sketch, "E173.13.endCap", {"start": v(514.15, 855.45) * mm, "mid": v(518.64, 855.6) * mm, "end": v(518.78, 851.1) * mm});
            skLineSegment(sketch, "E173.13.left", {"start": v(395.62, 729.25) * mm, "end": v(514.15, 855.45) * mm});
            skLineSegment(sketch, "E173.13.right", {"start": v(400.25, 724.9) * mm, "end": v(518.78, 851.1) * mm});
            skArc(sketch, "E173.14.startCap", {"start": v(476.13, 1492.83) * mm, "mid": v(480.62, 1492.97) * mm, "end": v(480.76, 1488.48) * mm});
            skArc(sketch, "E173.14.endCap", {"start": v(398, 1400.38) * mm, "mid": v(393.52, 1400.24) * mm, "end": v(393.38, 1404.72) * mm});
            skLineSegment(sketch, "E173.14.left", {"start": v(480.76, 1488.48) * mm, "end": v(398, 1400.38) * mm});
            skLineSegment(sketch, "E173.14.right", {"start": v(476.13, 1492.83) * mm, "end": v(393.38, 1404.72) * mm});
            skArc(sketch, "E173.15.startCap", {"start": v(514.15, 1137.24) * mm, "mid": v(518.64, 1137.38) * mm, "end": v(518.78, 1132.89) * mm});
            skArc(sketch, "E173.15.endCap", {"start": v(436.03, 1044.78) * mm, "mid": v(431.54, 1044.64) * mm, "end": v(431.4, 1049.13) * mm});
            skLineSegment(sketch, "E173.15.left", {"start": v(518.78, 1132.89) * mm, "end": v(436.03, 1044.78) * mm});
            skLineSegment(sketch, "E173.15.right", {"start": v(514.15, 1137.24) * mm, "end": v(431.4, 1049.13) * mm});
            skArc(sketch, "E173.16.startCap", {"start": v(400.25, 1044.78) * mm, "mid": v(395.76, 1044.64) * mm, "end": v(395.62, 1049.13) * mm});
            skArc(sketch, "E173.16.endCap", {"start": v(514.15, 1175.34) * mm, "mid": v(518.64, 1175.48) * mm, "end": v(518.78, 1170.99) * mm});
            skLineSegment(sketch, "E173.16.left", {"start": v(395.62, 1049.13) * mm, "end": v(514.15, 1175.34) * mm});
            skLineSegment(sketch, "E173.16.right", {"start": v(400.25, 1044.78) * mm, "end": v(518.78, 1170.99) * mm});
            skArc(sketch, "E173.17.startCap", {"start": v(699.44, 1172.95) * mm, "mid": v(703.92, 1173.1) * mm, "end": v(704.06, 1168.6) * mm});
            skArc(sketch, "E173.17.endCap", {"start": v(621.31, 1080.5) * mm, "mid": v(616.83, 1080.36) * mm, "end": v(616.69, 1084.84) * mm});
            skLineSegment(sketch, "E173.17.left", {"start": v(704.06, 1168.6) * mm, "end": v(621.31, 1080.5) * mm});
            skLineSegment(sketch, "E173.17.right", {"start": v(699.44, 1172.95) * mm, "end": v(616.69, 1084.84) * mm});
            skArc(sketch, "E173.18.startCap", {"start": v(252.82, 1812.71) * mm, "mid": v(257.3, 1812.85) * mm, "end": v(257.45, 1808.36) * mm});
            skArc(sketch, "E173.18.endCap", {"start": v(174.7, 1720.26) * mm, "mid": v(170.2, 1720.12) * mm, "end": v(170.07, 1724.6) * mm});
            skLineSegment(sketch, "E173.18.left", {"start": v(257.45, 1808.36) * mm, "end": v(174.7, 1720.26) * mm});
            skLineSegment(sketch, "E173.18.right", {"start": v(252.82, 1812.71) * mm, "end": v(170.07, 1724.6) * mm});
            skArc(sketch, "E173.19.startCap", {"start": v(176.94, 724.9) * mm, "mid": v(172.45, 724.76) * mm, "end": v(172.31, 729.25) * mm});
            skArc(sketch, "E173.19.endCap", {"start": v(290.84, 855.45) * mm, "mid": v(295.33, 855.6) * mm, "end": v(295.47, 851.1) * mm});
            skLineSegment(sketch, "E173.19.left", {"start": v(172.31, 729.25) * mm, "end": v(290.84, 855.45) * mm});
            skLineSegment(sketch, "E173.19.right", {"start": v(176.94, 724.9) * mm, "end": v(295.47, 851.1) * mm});
            skArc(sketch, "E173.20.startCap", {"start": v(290.84, 1137.24) * mm, "mid": v(295.33, 1137.38) * mm, "end": v(295.47, 1132.89) * mm});
            skArc(sketch, "E173.20.endCap", {"start": v(212.72, 1044.78) * mm, "mid": v(208.24, 1044.64) * mm, "end": v(208.1, 1049.13) * mm});
            skLineSegment(sketch, "E173.20.left", {"start": v(295.47, 1132.89) * mm, "end": v(212.72, 1044.78) * mm});
            skLineSegment(sketch, "E173.20.right", {"start": v(290.84, 1137.24) * mm, "end": v(208.1, 1049.13) * mm});
            skArc(sketch, "E173.21.startCap", {"start": v(400.25, 1364.66) * mm, "mid": v(395.76, 1364.52) * mm, "end": v(395.62, 1369.01) * mm});
            skArc(sketch, "E173.21.endCap", {"start": v(514.15, 1495.22) * mm, "mid": v(518.64, 1495.36) * mm, "end": v(518.78, 1490.87) * mm});
            skLineSegment(sketch, "E173.21.left", {"start": v(395.62, 1369.01) * mm, "end": v(514.15, 1495.22) * mm});
            skLineSegment(sketch, "E173.21.right", {"start": v(400.25, 1364.66) * mm, "end": v(518.78, 1490.87) * mm});
            skArc(sketch, "E173.22.startCap", {"start": v(737.46, 1457.12) * mm, "mid": v(741.95, 1457.26) * mm, "end": v(742.09, 1452.77) * mm});
            skArc(sketch, "E173.22.endCap", {"start": v(659.34, 1364.66) * mm, "mid": v(654.85, 1364.52) * mm, "end": v(654.71, 1369.01) * mm});
            skLineSegment(sketch, "E173.22.left", {"start": v(742.09, 1452.77) * mm, "end": v(659.34, 1364.66) * mm});
            skLineSegment(sketch, "E173.22.right", {"start": v(737.46, 1457.12) * mm, "end": v(654.71, 1369.01) * mm});
            skArc(sketch, "E173.23.startCap", {"start": v(737.46, 817.35) * mm, "mid": v(741.95, 817.5) * mm, "end": v(742.09, 813) * mm});
            skArc(sketch, "E173.23.endCap", {"start": v(659.34, 724.9) * mm, "mid": v(654.85, 724.76) * mm, "end": v(654.71, 729.25) * mm});
            skLineSegment(sketch, "E173.23.left", {"start": v(742.09, 813) * mm, "end": v(659.34, 724.9) * mm});
            skLineSegment(sketch, "E173.23.right", {"start": v(737.46, 817.35) * mm, "end": v(654.71, 729.25) * mm});
            skArc(sketch, "E173.24.startCap", {"start": v(737.46, 1137.24) * mm, "mid": v(741.95, 1137.38) * mm, "end": v(742.09, 1132.89) * mm});
            skArc(sketch, "E173.24.endCap", {"start": v(659.34, 1044.78) * mm, "mid": v(654.85, 1044.64) * mm, "end": v(654.71, 1049.13) * mm});
            skLineSegment(sketch, "E173.24.left", {"start": v(742.09, 1132.89) * mm, "end": v(659.34, 1044.78) * mm});
            skLineSegment(sketch, "E173.24.right", {"start": v(737.46, 1137.24) * mm, "end": v(654.71, 1049.13) * mm});
            skArc(sketch, "E173.25.startCap", {"start": v(623.56, 1364.66) * mm, "mid": v(619.07, 1364.52) * mm, "end": v(618.93, 1369.01) * mm});
            skArc(sketch, "E173.25.endCap", {"start": v(737.46, 1495.22) * mm, "mid": v(741.95, 1495.36) * mm, "end": v(742.09, 1490.87) * mm});
            skLineSegment(sketch, "E173.25.left", {"start": v(618.93, 1369.01) * mm, "end": v(737.46, 1495.22) * mm});
            skLineSegment(sketch, "E173.25.right", {"start": v(623.56, 1364.66) * mm, "end": v(742.09, 1490.87) * mm});
            skArc(sketch, "E173.26.startCap", {"start": v(699.44, 1492.83) * mm, "mid": v(703.92, 1492.97) * mm, "end": v(704.06, 1488.48) * mm});
            skArc(sketch, "E173.26.endCap", {"start": v(621.31, 1400.38) * mm, "mid": v(616.83, 1400.24) * mm, "end": v(616.69, 1404.72) * mm});
            skLineSegment(sketch, "E173.26.left", {"start": v(704.06, 1488.48) * mm, "end": v(621.31, 1400.38) * mm});
            skLineSegment(sketch, "E173.26.right", {"start": v(699.44, 1492.83) * mm, "end": v(616.69, 1404.72) * mm});
            skArc(sketch, "E173.27.startCap", {"start": v(252.82, 1172.95) * mm, "mid": v(257.3, 1173.1) * mm, "end": v(257.45, 1168.6) * mm});
            skArc(sketch, "E173.27.endCap", {"start": v(174.7, 1080.5) * mm, "mid": v(170.2, 1080.36) * mm, "end": v(170.07, 1084.84) * mm});
            skLineSegment(sketch, "E173.27.left", {"start": v(257.45, 1168.6) * mm, "end": v(174.7, 1080.5) * mm});
            skLineSegment(sketch, "E173.27.right", {"start": v(252.82, 1172.95) * mm, "end": v(170.07, 1084.84) * mm});
            skArc(sketch, "E173.28.startCap", {"start": v(623.56, 724.9) * mm, "mid": v(619.07, 724.76) * mm, "end": v(618.93, 729.25) * mm});
            skArc(sketch, "E173.28.endCap", {"start": v(737.46, 855.45) * mm, "mid": v(741.95, 855.6) * mm, "end": v(742.09, 851.1) * mm});
            skLineSegment(sketch, "E173.28.left", {"start": v(618.93, 729.25) * mm, "end": v(737.46, 855.45) * mm});
            skLineSegment(sketch, "E173.28.right", {"start": v(623.56, 724.9) * mm, "end": v(742.09, 851.1) * mm});
            skArc(sketch, "E173.29.startCap", {"start": v(514.15, 1457.12) * mm, "mid": v(518.64, 1457.26) * mm, "end": v(518.78, 1452.77) * mm});
            skArc(sketch, "E173.29.endCap", {"start": v(436.03, 1364.66) * mm, "mid": v(431.54, 1364.52) * mm, "end": v(431.4, 1369.01) * mm});
            skLineSegment(sketch, "E173.29.left", {"start": v(518.78, 1452.77) * mm, "end": v(436.03, 1364.66) * mm});
            skLineSegment(sketch, "E173.29.right", {"start": v(514.15, 1457.12) * mm, "end": v(431.4, 1369.01) * mm});
            skArc(sketch, "E173.30.startCap", {"start": v(252.82, 1492.83) * mm, "mid": v(257.3, 1492.97) * mm, "end": v(257.45, 1488.48) * mm});
            skArc(sketch, "E173.30.endCap", {"start": v(174.7, 1400.38) * mm, "mid": v(170.2, 1400.24) * mm, "end": v(170.07, 1404.72) * mm});
            skLineSegment(sketch, "E173.30.left", {"start": v(257.45, 1488.48) * mm, "end": v(174.7, 1400.38) * mm});
            skLineSegment(sketch, "E173.30.right", {"start": v(252.82, 1492.83) * mm, "end": v(170.07, 1404.72) * mm});
            skArc(sketch, "E173.31.startCap", {"start": v(290.84, 817.35) * mm, "mid": v(295.33, 817.5) * mm, "end": v(295.47, 813) * mm});
            skArc(sketch, "E173.31.endCap", {"start": v(212.72, 724.9) * mm, "mid": v(208.24, 724.76) * mm, "end": v(208.1, 729.25) * mm});
            skLineSegment(sketch, "E173.31.left", {"start": v(295.47, 813) * mm, "end": v(212.72, 724.9) * mm});
            skLineSegment(sketch, "E173.31.right", {"start": v(290.84, 817.35) * mm, "end": v(208.1, 729.25) * mm});
            skArc(sketch, "E173.32.startCap", {"start": v(623.56, 1044.78) * mm, "mid": v(619.07, 1044.64) * mm, "end": v(618.93, 1049.13) * mm});
            skArc(sketch, "E173.32.endCap", {"start": v(737.46, 1175.34) * mm, "mid": v(741.95, 1175.48) * mm, "end": v(742.09, 1170.99) * mm});
            skLineSegment(sketch, "E173.32.left", {"start": v(618.93, 1049.13) * mm, "end": v(737.46, 1175.34) * mm});
            skLineSegment(sketch, "E173.32.right", {"start": v(623.56, 1044.78) * mm, "end": v(742.09, 1170.99) * mm});
            skArc(sketch, "E173.33.startCap", {"start": v(252.82, 853.07) * mm, "mid": v(257.3, 853.2) * mm, "end": v(257.45, 848.72) * mm});
            skArc(sketch, "E173.33.endCap", {"start": v(174.7, 760.61) * mm, "mid": v(170.2, 760.47) * mm, "end": v(170.07, 764.96) * mm});
            skLineSegment(sketch, "E173.33.left", {"start": v(257.45, 848.72) * mm, "end": v(174.7, 760.61) * mm});
            skLineSegment(sketch, "E173.33.right", {"start": v(252.82, 853.07) * mm, "end": v(170.07, 764.96) * mm});
            skArc(sketch, "E173.34.startCap", {"start": v(176.94, 1044.78) * mm, "mid": v(172.45, 1044.64) * mm, "end": v(172.31, 1049.13) * mm});
            skArc(sketch, "E173.34.endCap", {"start": v(290.84, 1175.34) * mm, "mid": v(295.33, 1175.48) * mm, "end": v(295.47, 1170.99) * mm});
            skLineSegment(sketch, "E173.34.left", {"start": v(172.31, 1049.13) * mm, "end": v(290.84, 1175.34) * mm});
            skLineSegment(sketch, "E173.34.right", {"start": v(176.94, 1044.78) * mm, "end": v(295.47, 1170.99) * mm});
            skArc(sketch, "E173.35.startCap", {"start": v(476.13, 1172.95) * mm, "mid": v(480.62, 1173.1) * mm, "end": v(480.76, 1168.6) * mm});
            skArc(sketch, "E173.35.endCap", {"start": v(398, 1080.5) * mm, "mid": v(393.52, 1080.36) * mm, "end": v(393.38, 1084.84) * mm});
            skLineSegment(sketch, "E173.35.left", {"start": v(480.76, 1168.6) * mm, "end": v(398, 1080.5) * mm});
            skLineSegment(sketch, "E173.35.right", {"start": v(476.13, 1172.95) * mm, "end": v(393.38, 1084.84) * mm});
            skSolve(sketch);
        }
        {
            var Q0;
            Q0=qSketchRegion(id+"F9",true);
            extrude(context, id + "F10", {"entities" : qUnion([Q0]), "operationType" : NewBodyOperationType.REMOVE, "oppositeDirection" : true, "depth" : 25.4 * mm, "hasSecondDirection" : true, "secondDirectionOppositeDirection" : false, "secondDirectionDepth" : 31.75 * mm});
        }
        {
            var Q0;
            Q0=qCreatedBy(makeId("Front.planeOp"),FACE);
            var sketch = newSketch(context, id + "F11", { "sketchPlane" : qUnion([Q0])});
            skLineSegment(sketch, "E174.0.1", {"start": v(787.4, 254) * mm, "end": v(787.4, 542.93) * mm});
            skLineSegment(sketch, "E174.0.3", {"start": v(127, 542.93) * mm, "end": v(127, 254) * mm});
            skLineSegment(sketch, "E175.0", {"start": v(139.7, 266.7) * mm, "end": v(139.7, 530.22) * mm});
            skLineSegment(sketch, "E176.0", {"start": v(774.7, 266.7) * mm, "end": v(774.7, 530.22) * mm});
            skLineSegment(sketch, "E177", {"start": v(139.7, 530.22) * mm, "end": v(127, 542.93) * mm});
            skLineSegment(sketch, "E178", {"start": v(139.7, 266.7) * mm, "end": v(127, 254) * mm});
            skLineSegment(sketch, "E179", {"start": v(774.7, 266.7) * mm, "end": v(787.4, 254) * mm});
            skLineSegment(sketch, "E180", {"start": v(774.7, 530.22) * mm, "end": v(787.4, 542.93) * mm});
            skSolve(sketch);
        }
        {
            var Q0;
            Q0=qSketchRegion(id+"F11",true);
            extrude(context, id + "F12", {"entities" : qUnion([Q0]), "operationType" : NewBodyOperationType.ADD, "depth" : 20.02 * mm, "hasSecondDirection" : true, "secondDirectionOppositeDirection" : true, "secondDirectionDepth" : 20.02 * mm});
        }
        {
            var Q0;
            Q0=qCreatedBy(makeId("Front.planeOp"),FACE);
            var sketch = newSketch(context, id + "F13", { "sketchPlane" : qUnion([Q0])});
            skLineSegment(sketch, "E181.0", {"start": v(787.4, 542.93) * mm, "end": v(127, 542.93) * mm});
            skLineSegment(sketch, "E182.0", {"start": v(139.7, 530.22) * mm, "end": v(127, 542.93) * mm});
            skLineSegment(sketch, "E183.0", {"start": v(774.7, 530.22) * mm, "end": v(139.7, 530.22) * mm});
            skLineSegment(sketch, "E184.0", {"start": v(774.7, 530.22) * mm, "end": v(787.4, 542.93) * mm});
            skLineSegment(sketch, "E185.0", {"start": v(774.7, 266.7) * mm, "end": v(787.4, 254) * mm});
            skLineSegment(sketch, "E186.0", {"start": v(774.7, 266.7) * mm, "end": v(139.7, 266.7) * mm});
            skLineSegment(sketch, "E187.0", {"start": v(787.4, 254) * mm, "end": v(127, 254) * mm});
            skLineSegment(sketch, "E188.0", {"start": v(139.7, 266.7) * mm, "end": v(127, 254) * mm});
            skSolve(sketch);
        }
        {
            var Q0;
            Q0=qSketchRegion(id+"F13",true);
            extrude(context, id + "F14", {"entities" : qUnion([Q0]), "operationType" : NewBodyOperationType.ADD, "depth" : 19.05 * mm, "hasSecondDirection" : true, "secondDirectionOppositeDirection" : true, "secondDirectionDepth" : 19.05 * mm});
        }
        {
            var Q0;
            Q0=qCreatedBy(makeId("Front.planeOp"),FACE);
            var sketch = newSketch(context, id + "F15", { "sketchPlane" : qUnion([Q0])});
            skLineSegment(sketch, "E189.0.0", {"start": v(774.7, 266.7) * mm, "end": v(774.7, 530.22) * mm});
            skLineSegment(sketch, "E189.0.2", {"start": v(139.7, 530.22) * mm, "end": v(139.7, 266.7) * mm});
            skLineSegment(sketch, "E190.0", {"start": v(165.1, 292.1) * mm, "end": v(165.1, 504.83) * mm});
            skLineSegment(sketch, "E191.0", {"start": v(749.3, 292.1) * mm, "end": v(749.3, 504.83) * mm});
            skLineSegment(sketch, "E192", {"start": v(165.1, 292.1) * mm, "end": v(139.7, 266.7) * mm});
            skLineSegment(sketch, "E193", {"start": v(165.1, 504.83) * mm, "end": v(139.7, 530.22) * mm});
            skLineSegment(sketch, "E194", {"start": v(749.3, 504.83) * mm, "end": v(774.7, 530.22) * mm});
            skLineSegment(sketch, "E195", {"start": v(774.7, 266.7) * mm, "end": v(749.3, 292.1) * mm});
            skSolve(sketch);
        }
        {
            var Q0;
            Q0=qSketchRegion(id+"F15",true);
            extrude(context, id + "F16", {"entities" : qUnion([Q0]), "operationType" : NewBodyOperationType.ADD, "depth" : 17.78 * mm, "hasSecondDirection" : true, "secondDirectionOppositeDirection" : true, "secondDirectionDepth" : 17.78 * mm});
        }
        {
            var Q0;
            Q0=qCreatedBy(makeId("Front.planeOp"),FACE);
            var sketch = newSketch(context, id + "F17", { "sketchPlane" : qUnion([Q0])});
            skLineSegment(sketch, "E196.0", {"start": v(165.1, 504.83) * mm, "end": v(139.7, 530.22) * mm});
            skLineSegment(sketch, "E197.0", {"start": v(774.7, 530.22) * mm, "end": v(139.7, 530.22) * mm});
            skLineSegment(sketch, "E198.0", {"start": v(749.3, 504.83) * mm, "end": v(165.1, 504.83) * mm});
            skLineSegment(sketch, "E199.0", {"start": v(749.3, 504.83) * mm, "end": v(774.7, 530.22) * mm});
            skLineSegment(sketch, "E200.0", {"start": v(774.7, 266.7) * mm, "end": v(749.3, 292.1) * mm});
            skLineSegment(sketch, "E201.0", {"start": v(165.1, 292.1) * mm, "end": v(139.7, 266.7) * mm});
            skLineSegment(sketch, "E202.0", {"start": v(749.3, 292.1) * mm, "end": v(165.1, 292.1) * mm});
            skLineSegment(sketch, "E203.0", {"start": v(774.7, 266.7) * mm, "end": v(139.7, 266.7) * mm});
            skSolve(sketch);
        }
        {
            var Q0;
            Q0=qSketchRegion(id+"F17",true);
            extrude(context, id + "F18", {"entities" : qUnion([Q0]), "operationType" : NewBodyOperationType.ADD, "depth" : 16.5 * mm, "hasSecondDirection" : true, "secondDirectionOppositeDirection" : true, "secondDirectionDepth" : 16.5 * mm});
        }
        {
            var Q0;
            Q0=qCreatedBy(makeId("Front.planeOp"),FACE);
            var sketch = newSketch(context, id + "F19", { "sketchPlane" : qUnion([Q0])});
            skLineSegment(sketch, "E204.0.0", {"start": v(165.1, 292.1) * mm, "end": v(749.3, 292.1) * mm});
            skLineSegment(sketch, "E204.0.1", {"start": v(749.3, 292.1) * mm, "end": v(749.3, 504.83) * mm});
            skLineSegment(sketch, "E204.0.2", {"start": v(749.3, 504.83) * mm, "end": v(165.1, 504.83) * mm});
            skLineSegment(sketch, "E204.0.3", {"start": v(165.1, 504.83) * mm, "end": v(165.1, 292.1) * mm});
            skSolve(sketch);
        }
        {
            var Q0;
            Q0=qSketchRegion(id+"F19",true);
            extrude(context, id + "F20", {"entities" : qUnion([Q0]), "operationType" : NewBodyOperationType.ADD, "depth" : 6.35 * mm, "hasSecondDirection" : true, "secondDirectionOppositeDirection" : true, "secondDirectionDepth" : 6.35 * mm});
        }
    });
